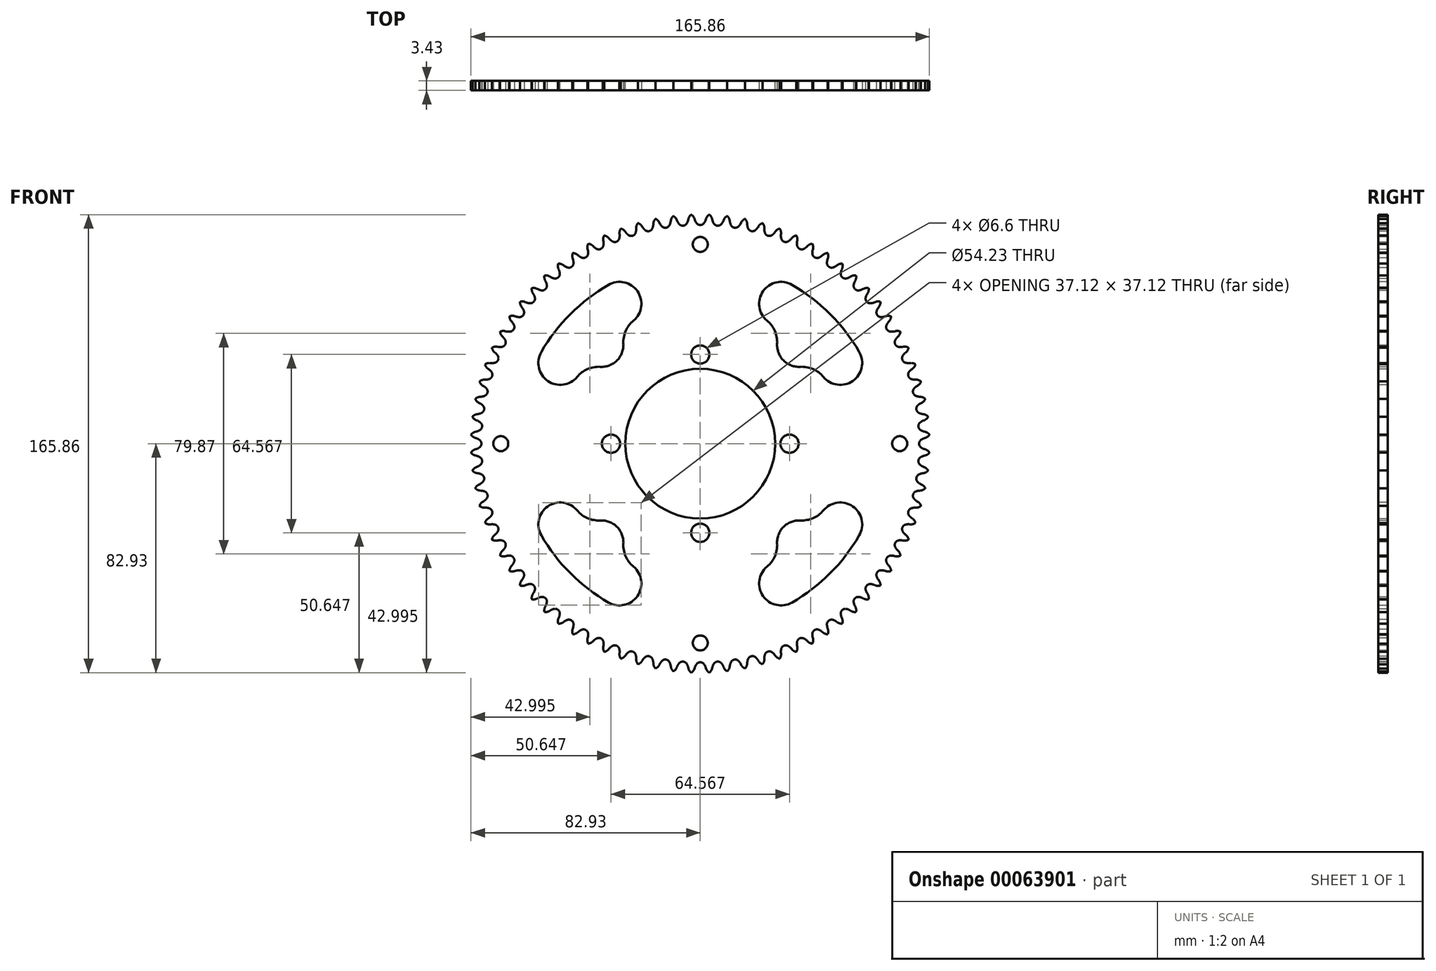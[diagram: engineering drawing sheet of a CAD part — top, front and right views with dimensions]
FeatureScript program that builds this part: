
annotation { "Feature Type Name" : "Feature", "Feature Type Description" : "" }
export const myFeature = defineFeature(function(context is Context, id is Id, definition is map)
    precondition{}
    {
        {
            var Q0;
            Q0=qCreatedBy(makeId("Front.planeOp"),FACE);
            var sketch = newSketch(context, id + "F0", { "sketchPlane" : qUnion([Q0])});
            skCircle(sketch, "E0", {"center": v(0, 0) * mm, "radius": 88.9 * mm});
            skCircle(sketch, "E1", {"center": v(0, 0) * mm, "radius": 27.11 * mm});
            skSolve(sketch);
        }
        {
            var Q0;
            Q0 = qSketchRegion(id + "F0", true);
            extrude(context, id + "F1", {"entities" : qUnion([Q0]), "depth" : 3.43 * mm});
        }
        {
            var Q0;
            Q0=makeQuery(id+"F1.opExtrude","CAP_FACE",FACE,{"disambiguationData":[OSD([sQuery(id+"F0.wireOp",EDGE,"E0"),sQuery(id+"F0.wireOp",EDGE,"E1")])],"isStart":false});
            var sketch = newSketch(context, id + "F2", { "sketchPlane" : qUnion([Q0])});
            skCircle(sketch, "E2", {"center": v(0, 0) * mm, "radius": 80.87 * mm, "construction": true});
            skLineSegment(sketch, "E3", {"start": v(0, 0) * mm, "end": v(0, 80.87) * mm, "construction": true});
            skLineSegment(sketch, "E4", {"start": v(0, 80.87) * mm, "end": v(106.86, 80.87) * mm, "construction": true});
            skLineSegment(sketch, "E5", {"start": v(0, 80.87) * mm, "end": v(2.14, 82.41) * mm, "construction": true});
            skLineSegment(sketch, "E6", {"start": v(2.14, 82.41) * mm, "end": v(-1.97, 81.04) * mm, "construction": true});
            skLineSegment(sketch, "E7", {"start": v(-1.97, 81.04) * mm, "end": v(-1.97, 81.04) * mm});
            skLineSegment(sketch, "E8", {"start": v(0, 0) * mm, "end": v(-3.26, 82.93) * mm, "construction": true});
            skPoint(sketch, "E8.endSnap0", {"position": v(-3.26, 84.9) * mm});
            skArc(sketch, "E9", {"start": v(-2.13, 81.52) * mm, "mid": v(-2.57, 82.33) * mm, "end": v(-3.26, 82.93) * mm});
            skArc(sketch, "E10", {"start": v(-3.26, 82.93) * mm, "mid": v(-6.67, 79.06) * mm, "end": v(-2.13, 81.52) * mm, "construction": true});
            skLineSegment(sketch, "E11", {"start": v(-2.13, 81.52) * mm, "end": v(-4.54, 88.75) * mm, "construction": true});
            skLineSegment(sketch, "E12", {"start": v(-1.97, 81.04) * mm, "end": v(-2.13, 81.52) * mm});
            skArc(sketch, "E13", {"start": v(-1.38, 79.88) * mm, "mid": v(6, 84.4) * mm, "end": v(-1.97, 81.04) * mm, "construction": true});
            skArc(sketch, "E14", {"start": v(-1.97, 81.04) * mm, "mid": v(-1.72, 80.44) * mm, "end": v(-1.38, 79.88) * mm});
            skArc(sketch, "E15.MirrorCS", {"start": v(1.38, 79.88) * mm, "mid": v(-6, 84.4) * mm, "end": v(1.97, 81.04) * mm, "construction": true});
            skArc(sketch, "E16.MirrorCS", {"start": v(2.13, 81.52) * mm, "mid": v(2.57, 82.33) * mm, "end": v(3.26, 82.93) * mm});
            skLineSegment(sketch, "E17.MirrorCS", {"start": v(1.97, 81.04) * mm, "end": v(2.13, 81.52) * mm});
            skArc(sketch, "E18.MirrorCS", {"start": v(1.97, 81.04) * mm, "mid": v(1.72, 80.44) * mm, "end": v(1.38, 79.88) * mm});
            skArc(sketch, "E19", {"start": v(-1.38, 79.88) * mm, "mid": v(0, 79.17) * mm, "end": v(1.38, 79.88) * mm});
            skArc(sketch, "E20", {"start": v(1.38, 79.88) * mm, "mid": v(0, 82.57) * mm, "end": v(-1.38, 79.88) * mm, "construction": true});
            skArc(sketch, "E21.1.0", {"start": v(-8.52, 81.1) * mm, "mid": v(-9.02, 81.87) * mm, "end": v(-9.76, 82.42) * mm});
            skLineSegment(sketch, "E21.1.1", {"start": v(-8.33, 80.64) * mm, "end": v(-8.52, 81.1) * mm});
            skArc(sketch, "E21.1.2", {"start": v(-8.33, 80.64) * mm, "mid": v(-8.03, 80.05) * mm, "end": v(-7.64, 79.52) * mm});
            skArc(sketch, "E21.1.3", {"start": v(-7.64, 79.52) * mm, "mid": v(-6.21, 78.93) * mm, "end": v(-4.9, 79.74) * mm});
            skArc(sketch, "E21.1.4", {"start": v(-4.4, 80.95) * mm, "mid": v(-4.6, 80.32) * mm, "end": v(-4.9, 79.74) * mm});
            skLineSegment(sketch, "E21.1.5", {"start": v(-4.4, 80.95) * mm, "end": v(-4.27, 81.44) * mm});
            skArc(sketch, "E21.1.6", {"start": v(-4.27, 81.44) * mm, "mid": v(-3.9, 82.27) * mm, "end": v(-3.26, 82.93) * mm});
            skArc(sketch, "E21.2.0", {"start": v(-14.86, 80.18) * mm, "mid": v(-15.42, 80.91) * mm, "end": v(-16.2, 81.4) * mm});
            skLineSegment(sketch, "E21.2.1", {"start": v(-14.63, 79.73) * mm, "end": v(-14.86, 80.18) * mm});
            skArc(sketch, "E21.2.2", {"start": v(-14.63, 79.73) * mm, "mid": v(-14.28, 79.18) * mm, "end": v(-13.86, 78.68) * mm});
            skArc(sketch, "E21.2.3", {"start": v(-13.86, 78.68) * mm, "mid": v(-12.39, 78.2) * mm, "end": v(-11.13, 79.11) * mm});
            skArc(sketch, "E21.2.4", {"start": v(-10.73, 80.35) * mm, "mid": v(-10.89, 79.72) * mm, "end": v(-11.13, 79.11) * mm});
            skLineSegment(sketch, "E21.2.5", {"start": v(-10.73, 80.35) * mm, "end": v(-10.65, 80.85) * mm});
            skArc(sketch, "E21.2.6", {"start": v(-10.65, 80.85) * mm, "mid": v(-10.34, 81.71) * mm, "end": v(-9.76, 82.42) * mm});
            skArc(sketch, "E21.3.0", {"start": v(-21.1, 78.77) * mm, "mid": v(-21.72, 79.45) * mm, "end": v(-22.53, 79.88) * mm});
            skLineSegment(sketch, "E21.3.1", {"start": v(-20.84, 78.34) * mm, "end": v(-21.1, 78.77) * mm});
            skArc(sketch, "E21.3.2", {"start": v(-20.84, 78.34) * mm, "mid": v(-20.45, 77.81) * mm, "end": v(-19.99, 77.35) * mm});
            skArc(sketch, "E21.3.3", {"start": v(-19.99, 77.35) * mm, "mid": v(-18.48, 76.99) * mm, "end": v(-17.3, 78) * mm});
            skArc(sketch, "E21.3.4", {"start": v(-17, 79.26) * mm, "mid": v(-17.1, 78.62) * mm, "end": v(-17.3, 78) * mm});
            skLineSegment(sketch, "E21.3.5", {"start": v(-17, 79.26) * mm, "end": v(-16.96, 79.77) * mm});
            skArc(sketch, "E21.3.6", {"start": v(-16.96, 79.77) * mm, "mid": v(-16.72, 80.65) * mm, "end": v(-16.2, 81.4) * mm});
            skArc(sketch, "E21.4.0", {"start": v(-27.22, 76.87) * mm, "mid": v(-27.88, 77.5) * mm, "end": v(-28.73, 77.87) * mm});
            skLineSegment(sketch, "E21.4.1", {"start": v(-26.92, 76.47) * mm, "end": v(-27.22, 76.87) * mm});
            skArc(sketch, "E21.4.2", {"start": v(-26.92, 76.47) * mm, "mid": v(-26.5, 75.97) * mm, "end": v(-26, 75.54) * mm});
            skArc(sketch, "E21.4.3", {"start": v(-26, 75.54) * mm, "mid": v(-24.47, 75.3) * mm, "end": v(-23.37, 76.4) * mm});
            skArc(sketch, "E21.4.4", {"start": v(-23.17, 77.68) * mm, "mid": v(-23.22, 77.03) * mm, "end": v(-23.37, 76.4) * mm});
            skLineSegment(sketch, "E21.4.5", {"start": v(-23.17, 77.68) * mm, "end": v(-23.16, 78.19) * mm});
            skArc(sketch, "E21.4.6", {"start": v(-23.16, 78.19) * mm, "mid": v(-23, 79.1) * mm, "end": v(-22.53, 79.88) * mm});
            skArc(sketch, "E21.5.0", {"start": v(-33.17, 74.5) * mm, "mid": v(-33.88, 75.08) * mm, "end": v(-34.75, 75.37) * mm});
            skLineSegment(sketch, "E21.5.1", {"start": v(-32.84, 74.12) * mm, "end": v(-33.17, 74.5) * mm});
            skArc(sketch, "E21.5.2", {"start": v(-32.84, 74.12) * mm, "mid": v(-32.37, 73.66) * mm, "end": v(-31.84, 73.27) * mm});
            skArc(sketch, "E21.5.3", {"start": v(-31.84, 73.27) * mm, "mid": v(-30.3, 73.15) * mm, "end": v(-29.3, 74.33) * mm});
            skArc(sketch, "E21.5.4", {"start": v(-29.2, 75.63) * mm, "mid": v(-29.2, 74.97) * mm, "end": v(-29.3, 74.33) * mm});
            skLineSegment(sketch, "E21.5.5", {"start": v(-29.2, 75.63) * mm, "end": v(-29.23, 76.13) * mm});
            skArc(sketch, "E21.5.6", {"start": v(-29.23, 76.13) * mm, "mid": v(-29.13, 77.04) * mm, "end": v(-28.73, 77.87) * mm});
            skArc(sketch, "E21.6.0", {"start": v(-38.9, 71.67) * mm, "mid": v(-39.67, 72.19) * mm, "end": v(-40.55, 72.41) * mm});
            skLineSegment(sketch, "E21.6.1", {"start": v(-38.55, 71.31) * mm, "end": v(-38.9, 71.67) * mm});
            skArc(sketch, "E21.6.2", {"start": v(-38.55, 71.31) * mm, "mid": v(-38.05, 70.89) * mm, "end": v(-37.5, 70.55) * mm});
            skArc(sketch, "E21.6.3", {"start": v(-37.5, 70.55) * mm, "mid": v(-35.94, 70.54) * mm, "end": v(-35.04, 71.8) * mm});
            skArc(sketch, "E21.6.4", {"start": v(-35.03, 73.1) * mm, "mid": v(-34.99, 72.45) * mm, "end": v(-35.04, 71.8) * mm});
            skLineSegment(sketch, "E21.6.5", {"start": v(-35.03, 73.1) * mm, "end": v(-35.1, 73.6) * mm});
            skArc(sketch, "E21.6.6", {"start": v(-35.1, 73.6) * mm, "mid": v(-35.09, 74.52) * mm, "end": v(-34.75, 75.37) * mm});
            skArc(sketch, "E21.7.0", {"start": v(-44.41, 68.4) * mm, "mid": v(-45.2, 68.85) * mm, "end": v(-46.11, 69) * mm});
            skLineSegment(sketch, "E21.7.1", {"start": v(-44.03, 68.07) * mm, "end": v(-44.41, 68.4) * mm});
            skArc(sketch, "E21.7.2", {"start": v(-44.03, 68.07) * mm, "mid": v(-43.5, 67.69) * mm, "end": v(-42.91, 67.39) * mm});
            skArc(sketch, "E21.7.3", {"start": v(-42.91, 67.39) * mm, "mid": v(-41.37, 67.5) * mm, "end": v(-40.56, 68.83) * mm});
            skArc(sketch, "E21.7.4", {"start": v(-40.66, 70.13) * mm, "mid": v(-40.56, 69.48) * mm, "end": v(-40.56, 68.83) * mm});
            skLineSegment(sketch, "E21.7.5", {"start": v(-40.66, 70.13) * mm, "end": v(-40.78, 70.62) * mm});
            skArc(sketch, "E21.7.6", {"start": v(-40.78, 70.62) * mm, "mid": v(-40.82, 71.54) * mm, "end": v(-40.55, 72.41) * mm});
            skArc(sketch, "E21.8.0", {"start": v(-49.64, 64.7) * mm, "mid": v(-50.47, 65.1) * mm, "end": v(-51.38, 65.18) * mm});
            skLineSegment(sketch, "E21.8.1", {"start": v(-49.23, 64.4) * mm, "end": v(-49.64, 64.7) * mm});
            skArc(sketch, "E21.8.2", {"start": v(-49.23, 64.4) * mm, "mid": v(-48.67, 64.06) * mm, "end": v(-48.07, 63.81) * mm});
            skArc(sketch, "E21.8.3", {"start": v(-48.07, 63.81) * mm, "mid": v(-46.54, 64.05) * mm, "end": v(-45.84, 65.43) * mm});
            skArc(sketch, "E21.8.4", {"start": v(-46.04, 66.72) * mm, "mid": v(-45.89, 66.09) * mm, "end": v(-45.84, 65.43) * mm});
            skLineSegment(sketch, "E21.8.5", {"start": v(-46.04, 66.72) * mm, "end": v(-46.2, 67.2) * mm});
            skArc(sketch, "E21.8.6", {"start": v(-46.2, 67.2) * mm, "mid": v(-46.31, 68.11) * mm, "end": v(-46.11, 69) * mm});
            skArc(sketch, "E21.9.0", {"start": v(-54.57, 60.6) * mm, "mid": v(-55.42, 60.93) * mm, "end": v(-56.34, 60.95) * mm});
            skLineSegment(sketch, "E21.9.1", {"start": v(-54.13, 60.34) * mm, "end": v(-54.57, 60.6) * mm});
            skArc(sketch, "E21.9.2", {"start": v(-54.13, 60.34) * mm, "mid": v(-53.55, 60.05) * mm, "end": v(-52.93, 59.85) * mm});
            skArc(sketch, "E21.9.3", {"start": v(-52.93, 59.85) * mm, "mid": v(-51.42, 60.2) * mm, "end": v(-50.83, 61.64) * mm});
            skArc(sketch, "E21.9.4", {"start": v(-51.13, 62.9) * mm, "mid": v(-50.93, 62.28) * mm, "end": v(-50.83, 61.64) * mm});
            skLineSegment(sketch, "E21.9.5", {"start": v(-51.13, 62.9) * mm, "end": v(-51.32, 63.37) * mm});
            skArc(sketch, "E21.9.6", {"start": v(-51.32, 63.37) * mm, "mid": v(-51.51, 64.27) * mm, "end": v(-51.38, 65.18) * mm});
            skArc(sketch, "E21.10.0", {"start": v(-59.15, 56.14) * mm, "mid": v(-60.03, 56.4) * mm, "end": v(-60.95, 56.34) * mm});
            skLineSegment(sketch, "E21.10.1", {"start": v(-58.7, 55.9) * mm, "end": v(-59.15, 56.14) * mm});
            skArc(sketch, "E21.10.2", {"start": v(-58.7, 55.9) * mm, "mid": v(-58.1, 55.66) * mm, "end": v(-57.46, 55.5) * mm});
            skArc(sketch, "E21.10.3", {"start": v(-57.46, 55.5) * mm, "mid": v(-55.98, 55.98) * mm, "end": v(-55.5, 57.46) * mm});
            skArc(sketch, "E21.10.4", {"start": v(-55.9, 58.7) * mm, "mid": v(-55.66, 58.1) * mm, "end": v(-55.5, 57.46) * mm});
            skLineSegment(sketch, "E21.10.5", {"start": v(-55.9, 58.7) * mm, "end": v(-56.14, 59.15) * mm});
            skArc(sketch, "E21.10.6", {"start": v(-56.14, 59.15) * mm, "mid": v(-56.4, 60.03) * mm, "end": v(-56.34, 60.95) * mm});
            skArc(sketch, "E21.11.0", {"start": v(-63.37, 51.32) * mm, "mid": v(-64.27, 51.51) * mm, "end": v(-65.18, 51.38) * mm});
            skLineSegment(sketch, "E21.11.1", {"start": v(-62.9, 51.13) * mm, "end": v(-63.37, 51.32) * mm});
            skArc(sketch, "E21.11.2", {"start": v(-62.9, 51.13) * mm, "mid": v(-62.28, 50.93) * mm, "end": v(-61.64, 50.83) * mm});
            skArc(sketch, "E21.11.3", {"start": v(-61.64, 50.83) * mm, "mid": v(-60.2, 51.42) * mm, "end": v(-59.85, 52.93) * mm});
            skArc(sketch, "E21.11.4", {"start": v(-60.34, 54.13) * mm, "mid": v(-60.05, 53.55) * mm, "end": v(-59.85, 52.93) * mm});
            skLineSegment(sketch, "E21.11.5", {"start": v(-60.34, 54.13) * mm, "end": v(-60.6, 54.57) * mm});
            skArc(sketch, "E21.11.6", {"start": v(-60.6, 54.57) * mm, "mid": v(-60.93, 55.42) * mm, "end": v(-60.95, 56.34) * mm});
            skArc(sketch, "E21.12.0", {"start": v(-67.2, 46.2) * mm, "mid": v(-68.11, 46.31) * mm, "end": v(-69, 46.11) * mm});
            skLineSegment(sketch, "E21.12.1", {"start": v(-66.72, 46.04) * mm, "end": v(-67.2, 46.2) * mm});
            skArc(sketch, "E21.12.2", {"start": v(-66.72, 46.04) * mm, "mid": v(-66.09, 45.89) * mm, "end": v(-65.43, 45.84) * mm});
            skArc(sketch, "E21.12.3", {"start": v(-65.43, 45.84) * mm, "mid": v(-64.05, 46.54) * mm, "end": v(-63.81, 48.07) * mm});
            skArc(sketch, "E21.12.4", {"start": v(-64.4, 49.23) * mm, "mid": v(-64.06, 48.67) * mm, "end": v(-63.81, 48.07) * mm});
            skLineSegment(sketch, "E21.12.5", {"start": v(-64.4, 49.23) * mm, "end": v(-64.7, 49.64) * mm});
            skArc(sketch, "E21.12.6", {"start": v(-64.7, 49.64) * mm, "mid": v(-65.1, 50.47) * mm, "end": v(-65.18, 51.38) * mm});
            skArc(sketch, "E21.13.0", {"start": v(-70.62, 40.78) * mm, "mid": v(-71.54, 40.82) * mm, "end": v(-72.41, 40.55) * mm});
            skLineSegment(sketch, "E21.13.1", {"start": v(-70.13, 40.66) * mm, "end": v(-70.62, 40.78) * mm});
            skArc(sketch, "E21.13.2", {"start": v(-70.13, 40.66) * mm, "mid": v(-69.48, 40.56) * mm, "end": v(-68.83, 40.56) * mm});
            skArc(sketch, "E21.13.3", {"start": v(-68.83, 40.56) * mm, "mid": v(-67.5, 41.37) * mm, "end": v(-67.39, 42.91) * mm});
            skArc(sketch, "E21.13.4", {"start": v(-68.07, 44.03) * mm, "mid": v(-67.69, 43.5) * mm, "end": v(-67.39, 42.91) * mm});
            skLineSegment(sketch, "E21.13.5", {"start": v(-68.07, 44.03) * mm, "end": v(-68.4, 44.41) * mm});
            skArc(sketch, "E21.13.6", {"start": v(-68.4, 44.41) * mm, "mid": v(-68.85, 45.2) * mm, "end": v(-69, 46.11) * mm});
            skArc(sketch, "E21.14.0", {"start": v(-73.6, 35.1) * mm, "mid": v(-74.52, 35.09) * mm, "end": v(-75.37, 34.75) * mm});
            skLineSegment(sketch, "E21.14.1", {"start": v(-73.1, 35.03) * mm, "end": v(-73.6, 35.1) * mm});
            skArc(sketch, "E21.14.2", {"start": v(-73.1, 35.03) * mm, "mid": v(-72.45, 34.99) * mm, "end": v(-71.8, 35.04) * mm});
            skArc(sketch, "E21.14.3", {"start": v(-71.8, 35.04) * mm, "mid": v(-70.54, 35.94) * mm, "end": v(-70.55, 37.5) * mm});
            skArc(sketch, "E21.14.4", {"start": v(-71.31, 38.55) * mm, "mid": v(-70.89, 38.05) * mm, "end": v(-70.55, 37.5) * mm});
            skLineSegment(sketch, "E21.14.5", {"start": v(-71.31, 38.55) * mm, "end": v(-71.67, 38.9) * mm});
            skArc(sketch, "E21.14.6", {"start": v(-71.67, 38.9) * mm, "mid": v(-72.19, 39.67) * mm, "end": v(-72.41, 40.55) * mm});
            skArc(sketch, "E21.15.0", {"start": v(-76.13, 29.23) * mm, "mid": v(-77.04, 29.13) * mm, "end": v(-77.87, 28.73) * mm});
            skLineSegment(sketch, "E21.15.1", {"start": v(-75.63, 29.2) * mm, "end": v(-76.13, 29.23) * mm});
            skArc(sketch, "E21.15.2", {"start": v(-75.63, 29.2) * mm, "mid": v(-74.97, 29.2) * mm, "end": v(-74.33, 29.3) * mm});
            skArc(sketch, "E21.15.3", {"start": v(-74.33, 29.3) * mm, "mid": v(-73.15, 30.3) * mm, "end": v(-73.27, 31.84) * mm});
            skArc(sketch, "E21.15.4", {"start": v(-74.12, 32.84) * mm, "mid": v(-73.66, 32.37) * mm, "end": v(-73.27, 31.84) * mm});
            skLineSegment(sketch, "E21.15.5", {"start": v(-74.12, 32.84) * mm, "end": v(-74.5, 33.17) * mm});
            skArc(sketch, "E21.15.6", {"start": v(-74.5, 33.17) * mm, "mid": v(-75.08, 33.88) * mm, "end": v(-75.37, 34.75) * mm});
            skArc(sketch, "E21.16.0", {"start": v(-78.19, 23.16) * mm, "mid": v(-79.1, 23) * mm, "end": v(-79.88, 22.53) * mm});
            skLineSegment(sketch, "E21.16.1", {"start": v(-77.68, 23.17) * mm, "end": v(-78.19, 23.16) * mm});
            skArc(sketch, "E21.16.2", {"start": v(-77.68, 23.17) * mm, "mid": v(-77.03, 23.22) * mm, "end": v(-76.4, 23.37) * mm});
            skArc(sketch, "E21.16.3", {"start": v(-76.4, 23.37) * mm, "mid": v(-75.3, 24.47) * mm, "end": v(-75.54, 26) * mm});
            skArc(sketch, "E21.16.4", {"start": v(-76.47, 26.92) * mm, "mid": v(-75.97, 26.5) * mm, "end": v(-75.54, 26) * mm});
            skLineSegment(sketch, "E21.16.5", {"start": v(-76.47, 26.92) * mm, "end": v(-76.87, 27.22) * mm});
            skArc(sketch, "E21.16.6", {"start": v(-76.87, 27.22) * mm, "mid": v(-77.5, 27.88) * mm, "end": v(-77.87, 28.73) * mm});
            skArc(sketch, "E21.17.0", {"start": v(-79.77, 16.96) * mm, "mid": v(-80.65, 16.72) * mm, "end": v(-81.4, 16.2) * mm});
            skLineSegment(sketch, "E21.17.1", {"start": v(-79.26, 17) * mm, "end": v(-79.77, 16.96) * mm});
            skArc(sketch, "E21.17.2", {"start": v(-79.26, 17) * mm, "mid": v(-78.62, 17.1) * mm, "end": v(-78, 17.3) * mm});
            skArc(sketch, "E21.17.3", {"start": v(-78, 17.3) * mm, "mid": v(-76.99, 18.48) * mm, "end": v(-77.35, 19.99) * mm});
            skArc(sketch, "E21.17.4", {"start": v(-78.34, 20.84) * mm, "mid": v(-77.81, 20.45) * mm, "end": v(-77.35, 19.99) * mm});
            skLineSegment(sketch, "E21.17.5", {"start": v(-78.34, 20.84) * mm, "end": v(-78.77, 21.1) * mm});
            skArc(sketch, "E21.17.6", {"start": v(-78.77, 21.1) * mm, "mid": v(-79.45, 21.72) * mm, "end": v(-79.88, 22.53) * mm});
            skArc(sketch, "E21.18.0", {"start": v(-80.85, 10.65) * mm, "mid": v(-81.71, 10.34) * mm, "end": v(-82.42, 9.76) * mm});
            skLineSegment(sketch, "E21.18.1", {"start": v(-80.35, 10.73) * mm, "end": v(-80.85, 10.65) * mm});
            skArc(sketch, "E21.18.2", {"start": v(-80.35, 10.73) * mm, "mid": v(-79.72, 10.89) * mm, "end": v(-79.11, 11.13) * mm});
            skArc(sketch, "E21.18.3", {"start": v(-79.11, 11.13) * mm, "mid": v(-78.2, 12.39) * mm, "end": v(-78.68, 13.86) * mm});
            skArc(sketch, "E21.18.4", {"start": v(-79.73, 14.63) * mm, "mid": v(-79.18, 14.28) * mm, "end": v(-78.68, 13.86) * mm});
            skLineSegment(sketch, "E21.18.5", {"start": v(-79.73, 14.63) * mm, "end": v(-80.18, 14.86) * mm});
            skArc(sketch, "E21.18.6", {"start": v(-80.18, 14.86) * mm, "mid": v(-80.91, 15.42) * mm, "end": v(-81.4, 16.2) * mm});
            skArc(sketch, "E21.19.0", {"start": v(-81.44, 4.27) * mm, "mid": v(-82.27, 3.9) * mm, "end": v(-82.93, 3.26) * mm});
            skLineSegment(sketch, "E21.19.1", {"start": v(-80.95, 4.4) * mm, "end": v(-81.44, 4.27) * mm});
            skArc(sketch, "E21.19.2", {"start": v(-80.95, 4.4) * mm, "mid": v(-80.32, 4.6) * mm, "end": v(-79.74, 4.9) * mm});
            skArc(sketch, "E21.19.3", {"start": v(-79.74, 4.9) * mm, "mid": v(-78.93, 6.21) * mm, "end": v(-79.52, 7.64) * mm});
            skArc(sketch, "E21.19.4", {"start": v(-80.64, 8.33) * mm, "mid": v(-80.05, 8.03) * mm, "end": v(-79.52, 7.64) * mm});
            skLineSegment(sketch, "E21.19.5", {"start": v(-80.64, 8.33) * mm, "end": v(-81.1, 8.52) * mm});
            skArc(sketch, "E21.19.6", {"start": v(-81.1, 8.52) * mm, "mid": v(-81.87, 9.02) * mm, "end": v(-82.42, 9.76) * mm});
            skArc(sketch, "E21.20.0", {"start": v(-81.52, -2.13) * mm, "mid": v(-82.33, -2.57) * mm, "end": v(-82.93, -3.26) * mm});
            skLineSegment(sketch, "E21.20.1", {"start": v(-81.04, -1.97) * mm, "end": v(-81.52, -2.13) * mm});
            skArc(sketch, "E21.20.2", {"start": v(-81.04, -1.97) * mm, "mid": v(-80.44, -1.72) * mm, "end": v(-79.88, -1.38) * mm});
            skArc(sketch, "E21.20.3", {"start": v(-79.88, -1.38) * mm, "mid": v(-79.17, 0) * mm, "end": v(-79.88, 1.38) * mm});
            skArc(sketch, "E21.20.4", {"start": v(-81.04, 1.97) * mm, "mid": v(-80.44, 1.72) * mm, "end": v(-79.88, 1.38) * mm});
            skLineSegment(sketch, "E21.20.5", {"start": v(-81.04, 1.97) * mm, "end": v(-81.52, 2.13) * mm});
            skArc(sketch, "E21.20.6", {"start": v(-81.52, 2.13) * mm, "mid": v(-82.33, 2.57) * mm, "end": v(-82.93, 3.26) * mm});
            skArc(sketch, "E21.21.0", {"start": v(-81.1, -8.52) * mm, "mid": v(-81.87, -9.02) * mm, "end": v(-82.42, -9.76) * mm});
            skLineSegment(sketch, "E21.21.1", {"start": v(-80.64, -8.33) * mm, "end": v(-81.1, -8.52) * mm});
            skArc(sketch, "E21.21.2", {"start": v(-80.64, -8.33) * mm, "mid": v(-80.05, -8.03) * mm, "end": v(-79.52, -7.64) * mm});
            skArc(sketch, "E21.21.3", {"start": v(-79.52, -7.64) * mm, "mid": v(-78.93, -6.21) * mm, "end": v(-79.74, -4.9) * mm});
            skArc(sketch, "E21.21.4", {"start": v(-80.95, -4.4) * mm, "mid": v(-80.32, -4.6) * mm, "end": v(-79.74, -4.9) * mm});
            skLineSegment(sketch, "E21.21.5", {"start": v(-80.95, -4.4) * mm, "end": v(-81.44, -4.27) * mm});
            skArc(sketch, "E21.21.6", {"start": v(-81.44, -4.27) * mm, "mid": v(-82.27, -3.9) * mm, "end": v(-82.93, -3.26) * mm});
            skArc(sketch, "E21.22.0", {"start": v(-80.18, -14.86) * mm, "mid": v(-80.91, -15.42) * mm, "end": v(-81.4, -16.2) * mm});
            skLineSegment(sketch, "E21.22.1", {"start": v(-79.73, -14.63) * mm, "end": v(-80.18, -14.86) * mm});
            skArc(sketch, "E21.22.2", {"start": v(-79.73, -14.63) * mm, "mid": v(-79.18, -14.28) * mm, "end": v(-78.68, -13.86) * mm});
            skArc(sketch, "E21.22.3", {"start": v(-78.68, -13.86) * mm, "mid": v(-78.2, -12.39) * mm, "end": v(-79.11, -11.13) * mm});
            skArc(sketch, "E21.22.4", {"start": v(-80.35, -10.73) * mm, "mid": v(-79.72, -10.89) * mm, "end": v(-79.11, -11.13) * mm});
            skLineSegment(sketch, "E21.22.5", {"start": v(-80.35, -10.73) * mm, "end": v(-80.85, -10.65) * mm});
            skArc(sketch, "E21.22.6", {"start": v(-80.85, -10.65) * mm, "mid": v(-81.71, -10.34) * mm, "end": v(-82.42, -9.76) * mm});
            skArc(sketch, "E21.23.0", {"start": v(-78.77, -21.1) * mm, "mid": v(-79.45, -21.72) * mm, "end": v(-79.88, -22.53) * mm});
            skLineSegment(sketch, "E21.23.1", {"start": v(-78.34, -20.84) * mm, "end": v(-78.77, -21.1) * mm});
            skArc(sketch, "E21.23.2", {"start": v(-78.34, -20.84) * mm, "mid": v(-77.81, -20.45) * mm, "end": v(-77.35, -19.99) * mm});
            skArc(sketch, "E21.23.3", {"start": v(-77.35, -19.99) * mm, "mid": v(-76.99, -18.48) * mm, "end": v(-78, -17.3) * mm});
            skArc(sketch, "E21.23.4", {"start": v(-79.26, -17) * mm, "mid": v(-78.62, -17.1) * mm, "end": v(-78, -17.3) * mm});
            skLineSegment(sketch, "E21.23.5", {"start": v(-79.26, -17) * mm, "end": v(-79.77, -16.96) * mm});
            skArc(sketch, "E21.23.6", {"start": v(-79.77, -16.96) * mm, "mid": v(-80.65, -16.72) * mm, "end": v(-81.4, -16.2) * mm});
            skArc(sketch, "E21.24.0", {"start": v(-76.87, -27.22) * mm, "mid": v(-77.5, -27.88) * mm, "end": v(-77.87, -28.73) * mm});
            skLineSegment(sketch, "E21.24.1", {"start": v(-76.47, -26.92) * mm, "end": v(-76.87, -27.22) * mm});
            skArc(sketch, "E21.24.2", {"start": v(-76.47, -26.92) * mm, "mid": v(-75.97, -26.5) * mm, "end": v(-75.54, -26) * mm});
            skArc(sketch, "E21.24.3", {"start": v(-75.54, -26) * mm, "mid": v(-75.3, -24.47) * mm, "end": v(-76.4, -23.37) * mm});
            skArc(sketch, "E21.24.4", {"start": v(-77.68, -23.17) * mm, "mid": v(-77.03, -23.22) * mm, "end": v(-76.4, -23.37) * mm});
            skLineSegment(sketch, "E21.24.5", {"start": v(-77.68, -23.17) * mm, "end": v(-78.19, -23.16) * mm});
            skArc(sketch, "E21.24.6", {"start": v(-78.19, -23.16) * mm, "mid": v(-79.1, -23) * mm, "end": v(-79.88, -22.53) * mm});
            skArc(sketch, "E21.25.0", {"start": v(-74.5, -33.17) * mm, "mid": v(-75.08, -33.88) * mm, "end": v(-75.37, -34.75) * mm});
            skLineSegment(sketch, "E21.25.1", {"start": v(-74.12, -32.84) * mm, "end": v(-74.5, -33.17) * mm});
            skArc(sketch, "E21.25.2", {"start": v(-74.12, -32.84) * mm, "mid": v(-73.66, -32.37) * mm, "end": v(-73.27, -31.84) * mm});
            skArc(sketch, "E21.25.3", {"start": v(-73.27, -31.84) * mm, "mid": v(-73.15, -30.3) * mm, "end": v(-74.33, -29.3) * mm});
            skArc(sketch, "E21.25.4", {"start": v(-75.63, -29.2) * mm, "mid": v(-74.97, -29.2) * mm, "end": v(-74.33, -29.3) * mm});
            skLineSegment(sketch, "E21.25.5", {"start": v(-75.63, -29.2) * mm, "end": v(-76.13, -29.23) * mm});
            skArc(sketch, "E21.25.6", {"start": v(-76.13, -29.23) * mm, "mid": v(-77.04, -29.13) * mm, "end": v(-77.87, -28.73) * mm});
            skArc(sketch, "E21.26.0", {"start": v(-71.67, -38.9) * mm, "mid": v(-72.19, -39.67) * mm, "end": v(-72.41, -40.55) * mm});
            skLineSegment(sketch, "E21.26.1", {"start": v(-71.31, -38.55) * mm, "end": v(-71.67, -38.9) * mm});
            skArc(sketch, "E21.26.2", {"start": v(-71.31, -38.55) * mm, "mid": v(-70.89, -38.05) * mm, "end": v(-70.55, -37.5) * mm});
            skArc(sketch, "E21.26.3", {"start": v(-70.55, -37.5) * mm, "mid": v(-70.54, -35.94) * mm, "end": v(-71.8, -35.04) * mm});
            skArc(sketch, "E21.26.4", {"start": v(-73.1, -35.03) * mm, "mid": v(-72.45, -34.99) * mm, "end": v(-71.8, -35.04) * mm});
            skLineSegment(sketch, "E21.26.5", {"start": v(-73.1, -35.03) * mm, "end": v(-73.6, -35.1) * mm});
            skArc(sketch, "E21.26.6", {"start": v(-73.6, -35.1) * mm, "mid": v(-74.52, -35.09) * mm, "end": v(-75.37, -34.75) * mm});
            skArc(sketch, "E21.27.0", {"start": v(-68.4, -44.41) * mm, "mid": v(-68.85, -45.2) * mm, "end": v(-69, -46.11) * mm});
            skLineSegment(sketch, "E21.27.1", {"start": v(-68.07, -44.03) * mm, "end": v(-68.4, -44.41) * mm});
            skArc(sketch, "E21.27.2", {"start": v(-68.07, -44.03) * mm, "mid": v(-67.69, -43.5) * mm, "end": v(-67.39, -42.91) * mm});
            skArc(sketch, "E21.27.3", {"start": v(-67.39, -42.91) * mm, "mid": v(-67.5, -41.37) * mm, "end": v(-68.83, -40.56) * mm});
            skArc(sketch, "E21.27.4", {"start": v(-70.13, -40.66) * mm, "mid": v(-69.48, -40.56) * mm, "end": v(-68.83, -40.56) * mm});
            skLineSegment(sketch, "E21.27.5", {"start": v(-70.13, -40.66) * mm, "end": v(-70.62, -40.78) * mm});
            skArc(sketch, "E21.27.6", {"start": v(-70.62, -40.78) * mm, "mid": v(-71.54, -40.82) * mm, "end": v(-72.41, -40.55) * mm});
            skArc(sketch, "E21.28.0", {"start": v(-64.7, -49.64) * mm, "mid": v(-65.1, -50.47) * mm, "end": v(-65.18, -51.38) * mm});
            skLineSegment(sketch, "E21.28.1", {"start": v(-64.4, -49.23) * mm, "end": v(-64.7, -49.64) * mm});
            skArc(sketch, "E21.28.2", {"start": v(-64.4, -49.23) * mm, "mid": v(-64.06, -48.67) * mm, "end": v(-63.81, -48.07) * mm});
            skArc(sketch, "E21.28.3", {"start": v(-63.81, -48.07) * mm, "mid": v(-64.05, -46.54) * mm, "end": v(-65.43, -45.84) * mm});
            skArc(sketch, "E21.28.4", {"start": v(-66.72, -46.04) * mm, "mid": v(-66.09, -45.89) * mm, "end": v(-65.43, -45.84) * mm});
            skLineSegment(sketch, "E21.28.5", {"start": v(-66.72, -46.04) * mm, "end": v(-67.2, -46.2) * mm});
            skArc(sketch, "E21.28.6", {"start": v(-67.2, -46.2) * mm, "mid": v(-68.11, -46.31) * mm, "end": v(-69, -46.11) * mm});
            skArc(sketch, "E21.29.0", {"start": v(-60.6, -54.57) * mm, "mid": v(-60.93, -55.42) * mm, "end": v(-60.95, -56.34) * mm});
            skLineSegment(sketch, "E21.29.1", {"start": v(-60.34, -54.13) * mm, "end": v(-60.6, -54.57) * mm});
            skArc(sketch, "E21.29.2", {"start": v(-60.34, -54.13) * mm, "mid": v(-60.05, -53.55) * mm, "end": v(-59.85, -52.93) * mm});
            skArc(sketch, "E21.29.3", {"start": v(-59.85, -52.93) * mm, "mid": v(-60.2, -51.42) * mm, "end": v(-61.64, -50.83) * mm});
            skArc(sketch, "E21.29.4", {"start": v(-62.9, -51.13) * mm, "mid": v(-62.28, -50.93) * mm, "end": v(-61.64, -50.83) * mm});
            skLineSegment(sketch, "E21.29.5", {"start": v(-62.9, -51.13) * mm, "end": v(-63.37, -51.32) * mm});
            skArc(sketch, "E21.29.6", {"start": v(-63.37, -51.32) * mm, "mid": v(-64.27, -51.51) * mm, "end": v(-65.18, -51.38) * mm});
            skArc(sketch, "E21.30.0", {"start": v(-56.14, -59.15) * mm, "mid": v(-56.4, -60.03) * mm, "end": v(-56.34, -60.95) * mm});
            skLineSegment(sketch, "E21.30.1", {"start": v(-55.9, -58.7) * mm, "end": v(-56.14, -59.15) * mm});
            skArc(sketch, "E21.30.2", {"start": v(-55.9, -58.7) * mm, "mid": v(-55.66, -58.1) * mm, "end": v(-55.5, -57.46) * mm});
            skArc(sketch, "E21.30.3", {"start": v(-55.5, -57.46) * mm, "mid": v(-55.98, -55.98) * mm, "end": v(-57.46, -55.5) * mm});
            skArc(sketch, "E21.30.4", {"start": v(-58.7, -55.9) * mm, "mid": v(-58.1, -55.66) * mm, "end": v(-57.46, -55.5) * mm});
            skLineSegment(sketch, "E21.30.5", {"start": v(-58.7, -55.9) * mm, "end": v(-59.15, -56.14) * mm});
            skArc(sketch, "E21.30.6", {"start": v(-59.15, -56.14) * mm, "mid": v(-60.03, -56.4) * mm, "end": v(-60.95, -56.34) * mm});
            skArc(sketch, "E21.31.0", {"start": v(-51.32, -63.37) * mm, "mid": v(-51.51, -64.27) * mm, "end": v(-51.38, -65.18) * mm});
            skLineSegment(sketch, "E21.31.1", {"start": v(-51.13, -62.9) * mm, "end": v(-51.32, -63.37) * mm});
            skArc(sketch, "E21.31.2", {"start": v(-51.13, -62.9) * mm, "mid": v(-50.93, -62.28) * mm, "end": v(-50.83, -61.64) * mm});
            skArc(sketch, "E21.31.3", {"start": v(-50.83, -61.64) * mm, "mid": v(-51.42, -60.2) * mm, "end": v(-52.93, -59.85) * mm});
            skArc(sketch, "E21.31.4", {"start": v(-54.13, -60.34) * mm, "mid": v(-53.55, -60.05) * mm, "end": v(-52.93, -59.85) * mm});
            skLineSegment(sketch, "E21.31.5", {"start": v(-54.13, -60.34) * mm, "end": v(-54.57, -60.6) * mm});
            skArc(sketch, "E21.31.6", {"start": v(-54.57, -60.6) * mm, "mid": v(-55.42, -60.93) * mm, "end": v(-56.34, -60.95) * mm});
            skArc(sketch, "E21.32.0", {"start": v(-46.2, -67.2) * mm, "mid": v(-46.31, -68.11) * mm, "end": v(-46.11, -69) * mm});
            skLineSegment(sketch, "E21.32.1", {"start": v(-46.04, -66.72) * mm, "end": v(-46.2, -67.2) * mm});
            skArc(sketch, "E21.32.2", {"start": v(-46.04, -66.72) * mm, "mid": v(-45.89, -66.09) * mm, "end": v(-45.84, -65.43) * mm});
            skArc(sketch, "E21.32.3", {"start": v(-45.84, -65.43) * mm, "mid": v(-46.54, -64.05) * mm, "end": v(-48.07, -63.81) * mm});
            skArc(sketch, "E21.32.4", {"start": v(-49.23, -64.4) * mm, "mid": v(-48.67, -64.06) * mm, "end": v(-48.07, -63.81) * mm});
            skLineSegment(sketch, "E21.32.5", {"start": v(-49.23, -64.4) * mm, "end": v(-49.64, -64.7) * mm});
            skArc(sketch, "E21.32.6", {"start": v(-49.64, -64.7) * mm, "mid": v(-50.47, -65.1) * mm, "end": v(-51.38, -65.18) * mm});
            skArc(sketch, "E21.33.0", {"start": v(-40.78, -70.62) * mm, "mid": v(-40.82, -71.54) * mm, "end": v(-40.55, -72.41) * mm});
            skLineSegment(sketch, "E21.33.1", {"start": v(-40.66, -70.13) * mm, "end": v(-40.78, -70.62) * mm});
            skArc(sketch, "E21.33.2", {"start": v(-40.66, -70.13) * mm, "mid": v(-40.56, -69.48) * mm, "end": v(-40.56, -68.83) * mm});
            skArc(sketch, "E21.33.3", {"start": v(-40.56, -68.83) * mm, "mid": v(-41.37, -67.5) * mm, "end": v(-42.91, -67.39) * mm});
            skArc(sketch, "E21.33.4", {"start": v(-44.03, -68.07) * mm, "mid": v(-43.5, -67.69) * mm, "end": v(-42.91, -67.39) * mm});
            skLineSegment(sketch, "E21.33.5", {"start": v(-44.03, -68.07) * mm, "end": v(-44.41, -68.4) * mm});
            skArc(sketch, "E21.33.6", {"start": v(-44.41, -68.4) * mm, "mid": v(-45.2, -68.85) * mm, "end": v(-46.11, -69) * mm});
            skArc(sketch, "E21.34.0", {"start": v(-35.1, -73.6) * mm, "mid": v(-35.09, -74.52) * mm, "end": v(-34.75, -75.37) * mm});
            skLineSegment(sketch, "E21.34.1", {"start": v(-35.03, -73.1) * mm, "end": v(-35.1, -73.6) * mm});
            skArc(sketch, "E21.34.2", {"start": v(-35.03, -73.1) * mm, "mid": v(-34.99, -72.45) * mm, "end": v(-35.04, -71.8) * mm});
            skArc(sketch, "E21.34.3", {"start": v(-35.04, -71.8) * mm, "mid": v(-35.94, -70.54) * mm, "end": v(-37.5, -70.55) * mm});
            skArc(sketch, "E21.34.4", {"start": v(-38.55, -71.31) * mm, "mid": v(-38.05, -70.89) * mm, "end": v(-37.5, -70.55) * mm});
            skLineSegment(sketch, "E21.34.5", {"start": v(-38.55, -71.31) * mm, "end": v(-38.9, -71.67) * mm});
            skArc(sketch, "E21.34.6", {"start": v(-38.9, -71.67) * mm, "mid": v(-39.67, -72.19) * mm, "end": v(-40.55, -72.41) * mm});
            skArc(sketch, "E21.35.0", {"start": v(-29.23, -76.13) * mm, "mid": v(-29.13, -77.04) * mm, "end": v(-28.73, -77.87) * mm});
            skLineSegment(sketch, "E21.35.1", {"start": v(-29.2, -75.63) * mm, "end": v(-29.23, -76.13) * mm});
            skArc(sketch, "E21.35.2", {"start": v(-29.2, -75.63) * mm, "mid": v(-29.2, -74.97) * mm, "end": v(-29.3, -74.33) * mm});
            skArc(sketch, "E21.35.3", {"start": v(-29.3, -74.33) * mm, "mid": v(-30.3, -73.15) * mm, "end": v(-31.84, -73.27) * mm});
            skArc(sketch, "E21.35.4", {"start": v(-32.84, -74.12) * mm, "mid": v(-32.37, -73.66) * mm, "end": v(-31.84, -73.27) * mm});
            skLineSegment(sketch, "E21.35.5", {"start": v(-32.84, -74.12) * mm, "end": v(-33.17, -74.5) * mm});
            skArc(sketch, "E21.35.6", {"start": v(-33.17, -74.5) * mm, "mid": v(-33.88, -75.08) * mm, "end": v(-34.75, -75.37) * mm});
            skArc(sketch, "E21.36.0", {"start": v(-23.16, -78.19) * mm, "mid": v(-23, -79.1) * mm, "end": v(-22.53, -79.88) * mm});
            skLineSegment(sketch, "E21.36.1", {"start": v(-23.17, -77.68) * mm, "end": v(-23.16, -78.19) * mm});
            skArc(sketch, "E21.36.2", {"start": v(-23.17, -77.68) * mm, "mid": v(-23.22, -77.03) * mm, "end": v(-23.37, -76.4) * mm});
            skArc(sketch, "E21.36.3", {"start": v(-23.37, -76.4) * mm, "mid": v(-24.47, -75.3) * mm, "end": v(-26, -75.54) * mm});
            skArc(sketch, "E21.36.4", {"start": v(-26.92, -76.47) * mm, "mid": v(-26.5, -75.97) * mm, "end": v(-26, -75.54) * mm});
            skLineSegment(sketch, "E21.36.5", {"start": v(-26.92, -76.47) * mm, "end": v(-27.22, -76.87) * mm});
            skArc(sketch, "E21.36.6", {"start": v(-27.22, -76.87) * mm, "mid": v(-27.88, -77.5) * mm, "end": v(-28.73, -77.87) * mm});
            skArc(sketch, "E21.37.0", {"start": v(-16.96, -79.77) * mm, "mid": v(-16.72, -80.65) * mm, "end": v(-16.2, -81.4) * mm});
            skLineSegment(sketch, "E21.37.1", {"start": v(-17, -79.26) * mm, "end": v(-16.96, -79.77) * mm});
            skArc(sketch, "E21.37.2", {"start": v(-17, -79.26) * mm, "mid": v(-17.1, -78.62) * mm, "end": v(-17.3, -78) * mm});
            skArc(sketch, "E21.37.3", {"start": v(-17.3, -78) * mm, "mid": v(-18.48, -76.99) * mm, "end": v(-19.99, -77.35) * mm});
            skArc(sketch, "E21.37.4", {"start": v(-20.84, -78.34) * mm, "mid": v(-20.45, -77.81) * mm, "end": v(-19.99, -77.35) * mm});
            skLineSegment(sketch, "E21.37.5", {"start": v(-20.84, -78.34) * mm, "end": v(-21.1, -78.77) * mm});
            skArc(sketch, "E21.37.6", {"start": v(-21.1, -78.77) * mm, "mid": v(-21.72, -79.45) * mm, "end": v(-22.53, -79.88) * mm});
            skArc(sketch, "E21.38.0", {"start": v(-10.65, -80.85) * mm, "mid": v(-10.34, -81.71) * mm, "end": v(-9.76, -82.42) * mm});
            skLineSegment(sketch, "E21.38.1", {"start": v(-10.73, -80.35) * mm, "end": v(-10.65, -80.85) * mm});
            skArc(sketch, "E21.38.2", {"start": v(-10.73, -80.35) * mm, "mid": v(-10.89, -79.72) * mm, "end": v(-11.13, -79.11) * mm});
            skArc(sketch, "E21.38.3", {"start": v(-11.13, -79.11) * mm, "mid": v(-12.39, -78.2) * mm, "end": v(-13.86, -78.68) * mm});
            skArc(sketch, "E21.38.4", {"start": v(-14.63, -79.73) * mm, "mid": v(-14.28, -79.18) * mm, "end": v(-13.86, -78.68) * mm});
            skLineSegment(sketch, "E21.38.5", {"start": v(-14.63, -79.73) * mm, "end": v(-14.86, -80.18) * mm});
            skArc(sketch, "E21.38.6", {"start": v(-14.86, -80.18) * mm, "mid": v(-15.42, -80.91) * mm, "end": v(-16.2, -81.4) * mm});
            skArc(sketch, "E21.39.0", {"start": v(-4.27, -81.44) * mm, "mid": v(-3.9, -82.27) * mm, "end": v(-3.26, -82.93) * mm});
            skLineSegment(sketch, "E21.39.1", {"start": v(-4.4, -80.95) * mm, "end": v(-4.27, -81.44) * mm});
            skArc(sketch, "E21.39.2", {"start": v(-4.4, -80.95) * mm, "mid": v(-4.6, -80.32) * mm, "end": v(-4.9, -79.74) * mm});
            skArc(sketch, "E21.39.3", {"start": v(-4.9, -79.74) * mm, "mid": v(-6.21, -78.93) * mm, "end": v(-7.64, -79.52) * mm});
            skArc(sketch, "E21.39.4", {"start": v(-8.33, -80.64) * mm, "mid": v(-8.03, -80.05) * mm, "end": v(-7.64, -79.52) * mm});
            skLineSegment(sketch, "E21.39.5", {"start": v(-8.33, -80.64) * mm, "end": v(-8.52, -81.1) * mm});
            skArc(sketch, "E21.39.6", {"start": v(-8.52, -81.1) * mm, "mid": v(-9.02, -81.87) * mm, "end": v(-9.76, -82.42) * mm});
            skArc(sketch, "E21.40.0", {"start": v(2.13, -81.52) * mm, "mid": v(2.57, -82.33) * mm, "end": v(3.26, -82.93) * mm});
            skLineSegment(sketch, "E21.40.1", {"start": v(1.97, -81.04) * mm, "end": v(2.13, -81.52) * mm});
            skArc(sketch, "E21.40.2", {"start": v(1.97, -81.04) * mm, "mid": v(1.72, -80.44) * mm, "end": v(1.38, -79.88) * mm});
            skArc(sketch, "E21.40.3", {"start": v(1.38, -79.88) * mm, "mid": v(0, -79.17) * mm, "end": v(-1.38, -79.88) * mm});
            skArc(sketch, "E21.40.4", {"start": v(-1.97, -81.04) * mm, "mid": v(-1.72, -80.44) * mm, "end": v(-1.38, -79.88) * mm});
            skLineSegment(sketch, "E21.40.5", {"start": v(-1.97, -81.04) * mm, "end": v(-2.13, -81.52) * mm});
            skArc(sketch, "E21.40.6", {"start": v(-2.13, -81.52) * mm, "mid": v(-2.57, -82.33) * mm, "end": v(-3.26, -82.93) * mm});
            skArc(sketch, "E21.41.0", {"start": v(8.52, -81.1) * mm, "mid": v(9.02, -81.87) * mm, "end": v(9.76, -82.42) * mm});
            skLineSegment(sketch, "E21.41.1", {"start": v(8.33, -80.64) * mm, "end": v(8.52, -81.1) * mm});
            skArc(sketch, "E21.41.2", {"start": v(8.33, -80.64) * mm, "mid": v(8.03, -80.05) * mm, "end": v(7.64, -79.52) * mm});
            skArc(sketch, "E21.41.3", {"start": v(7.64, -79.52) * mm, "mid": v(6.21, -78.93) * mm, "end": v(4.9, -79.74) * mm});
            skArc(sketch, "E21.41.4", {"start": v(4.4, -80.95) * mm, "mid": v(4.6, -80.32) * mm, "end": v(4.9, -79.74) * mm});
            skLineSegment(sketch, "E21.41.5", {"start": v(4.4, -80.95) * mm, "end": v(4.27, -81.44) * mm});
            skArc(sketch, "E21.41.6", {"start": v(4.27, -81.44) * mm, "mid": v(3.9, -82.27) * mm, "end": v(3.26, -82.93) * mm});
            skArc(sketch, "E21.42.0", {"start": v(14.86, -80.18) * mm, "mid": v(15.42, -80.91) * mm, "end": v(16.2, -81.4) * mm});
            skLineSegment(sketch, "E21.42.1", {"start": v(14.63, -79.73) * mm, "end": v(14.86, -80.18) * mm});
            skArc(sketch, "E21.42.2", {"start": v(14.63, -79.73) * mm, "mid": v(14.28, -79.18) * mm, "end": v(13.86, -78.68) * mm});
            skArc(sketch, "E21.42.3", {"start": v(13.86, -78.68) * mm, "mid": v(12.39, -78.2) * mm, "end": v(11.13, -79.11) * mm});
            skArc(sketch, "E21.42.4", {"start": v(10.73, -80.35) * mm, "mid": v(10.89, -79.72) * mm, "end": v(11.13, -79.11) * mm});
            skLineSegment(sketch, "E21.42.5", {"start": v(10.73, -80.35) * mm, "end": v(10.65, -80.85) * mm});
            skArc(sketch, "E21.42.6", {"start": v(10.65, -80.85) * mm, "mid": v(10.34, -81.71) * mm, "end": v(9.76, -82.42) * mm});
            skArc(sketch, "E21.43.0", {"start": v(21.1, -78.77) * mm, "mid": v(21.72, -79.45) * mm, "end": v(22.53, -79.88) * mm});
            skLineSegment(sketch, "E21.43.1", {"start": v(20.84, -78.34) * mm, "end": v(21.1, -78.77) * mm});
            skArc(sketch, "E21.43.2", {"start": v(20.84, -78.34) * mm, "mid": v(20.45, -77.81) * mm, "end": v(19.99, -77.35) * mm});
            skArc(sketch, "E21.43.3", {"start": v(19.99, -77.35) * mm, "mid": v(18.48, -76.99) * mm, "end": v(17.3, -78) * mm});
            skArc(sketch, "E21.43.4", {"start": v(17, -79.26) * mm, "mid": v(17.1, -78.62) * mm, "end": v(17.3, -78) * mm});
            skLineSegment(sketch, "E21.43.5", {"start": v(17, -79.26) * mm, "end": v(16.96, -79.77) * mm});
            skArc(sketch, "E21.43.6", {"start": v(16.96, -79.77) * mm, "mid": v(16.72, -80.65) * mm, "end": v(16.2, -81.4) * mm});
            skArc(sketch, "E21.44.0", {"start": v(27.22, -76.87) * mm, "mid": v(27.88, -77.5) * mm, "end": v(28.73, -77.87) * mm});
            skLineSegment(sketch, "E21.44.1", {"start": v(26.92, -76.47) * mm, "end": v(27.22, -76.87) * mm});
            skArc(sketch, "E21.44.2", {"start": v(26.92, -76.47) * mm, "mid": v(26.5, -75.97) * mm, "end": v(26, -75.54) * mm});
            skArc(sketch, "E21.44.3", {"start": v(26, -75.54) * mm, "mid": v(24.47, -75.3) * mm, "end": v(23.37, -76.4) * mm});
            skArc(sketch, "E21.44.4", {"start": v(23.17, -77.68) * mm, "mid": v(23.22, -77.03) * mm, "end": v(23.37, -76.4) * mm});
            skLineSegment(sketch, "E21.44.5", {"start": v(23.17, -77.68) * mm, "end": v(23.16, -78.19) * mm});
            skArc(sketch, "E21.44.6", {"start": v(23.16, -78.19) * mm, "mid": v(23, -79.1) * mm, "end": v(22.53, -79.88) * mm});
            skArc(sketch, "E21.45.0", {"start": v(33.17, -74.5) * mm, "mid": v(33.88, -75.08) * mm, "end": v(34.75, -75.37) * mm});
            skLineSegment(sketch, "E21.45.1", {"start": v(32.84, -74.12) * mm, "end": v(33.17, -74.5) * mm});
            skArc(sketch, "E21.45.2", {"start": v(32.84, -74.12) * mm, "mid": v(32.37, -73.66) * mm, "end": v(31.84, -73.27) * mm});
            skArc(sketch, "E21.45.3", {"start": v(31.84, -73.27) * mm, "mid": v(30.3, -73.15) * mm, "end": v(29.3, -74.33) * mm});
            skArc(sketch, "E21.45.4", {"start": v(29.2, -75.63) * mm, "mid": v(29.2, -74.97) * mm, "end": v(29.3, -74.33) * mm});
            skLineSegment(sketch, "E21.45.5", {"start": v(29.2, -75.63) * mm, "end": v(29.23, -76.13) * mm});
            skArc(sketch, "E21.45.6", {"start": v(29.23, -76.13) * mm, "mid": v(29.13, -77.04) * mm, "end": v(28.73, -77.87) * mm});
            skArc(sketch, "E21.46.0", {"start": v(38.9, -71.67) * mm, "mid": v(39.67, -72.19) * mm, "end": v(40.55, -72.41) * mm});
            skLineSegment(sketch, "E21.46.1", {"start": v(38.55, -71.31) * mm, "end": v(38.9, -71.67) * mm});
            skArc(sketch, "E21.46.2", {"start": v(38.55, -71.31) * mm, "mid": v(38.05, -70.89) * mm, "end": v(37.5, -70.55) * mm});
            skArc(sketch, "E21.46.3", {"start": v(37.5, -70.55) * mm, "mid": v(35.94, -70.54) * mm, "end": v(35.04, -71.8) * mm});
            skArc(sketch, "E21.46.4", {"start": v(35.03, -73.1) * mm, "mid": v(34.99, -72.45) * mm, "end": v(35.04, -71.8) * mm});
            skLineSegment(sketch, "E21.46.5", {"start": v(35.03, -73.1) * mm, "end": v(35.1, -73.6) * mm});
            skArc(sketch, "E21.46.6", {"start": v(35.1, -73.6) * mm, "mid": v(35.09, -74.52) * mm, "end": v(34.75, -75.37) * mm});
            skArc(sketch, "E21.47.0", {"start": v(44.41, -68.4) * mm, "mid": v(45.2, -68.85) * mm, "end": v(46.11, -69) * mm});
            skLineSegment(sketch, "E21.47.1", {"start": v(44.03, -68.07) * mm, "end": v(44.41, -68.4) * mm});
            skArc(sketch, "E21.47.2", {"start": v(44.03, -68.07) * mm, "mid": v(43.5, -67.69) * mm, "end": v(42.91, -67.39) * mm});
            skArc(sketch, "E21.47.3", {"start": v(42.91, -67.39) * mm, "mid": v(41.37, -67.5) * mm, "end": v(40.56, -68.83) * mm});
            skArc(sketch, "E21.47.4", {"start": v(40.66, -70.13) * mm, "mid": v(40.56, -69.48) * mm, "end": v(40.56, -68.83) * mm});
            skLineSegment(sketch, "E21.47.5", {"start": v(40.66, -70.13) * mm, "end": v(40.78, -70.62) * mm});
            skArc(sketch, "E21.47.6", {"start": v(40.78, -70.62) * mm, "mid": v(40.82, -71.54) * mm, "end": v(40.55, -72.41) * mm});
            skArc(sketch, "E21.48.0", {"start": v(49.64, -64.7) * mm, "mid": v(50.47, -65.1) * mm, "end": v(51.38, -65.18) * mm});
            skLineSegment(sketch, "E21.48.1", {"start": v(49.23, -64.4) * mm, "end": v(49.64, -64.7) * mm});
            skArc(sketch, "E21.48.2", {"start": v(49.23, -64.4) * mm, "mid": v(48.67, -64.06) * mm, "end": v(48.07, -63.81) * mm});
            skArc(sketch, "E21.48.3", {"start": v(48.07, -63.81) * mm, "mid": v(46.54, -64.05) * mm, "end": v(45.84, -65.43) * mm});
            skArc(sketch, "E21.48.4", {"start": v(46.04, -66.72) * mm, "mid": v(45.89, -66.09) * mm, "end": v(45.84, -65.43) * mm});
            skLineSegment(sketch, "E21.48.5", {"start": v(46.04, -66.72) * mm, "end": v(46.2, -67.2) * mm});
            skArc(sketch, "E21.48.6", {"start": v(46.2, -67.2) * mm, "mid": v(46.31, -68.11) * mm, "end": v(46.11, -69) * mm});
            skArc(sketch, "E21.49.0", {"start": v(54.57, -60.6) * mm, "mid": v(55.42, -60.93) * mm, "end": v(56.34, -60.95) * mm});
            skLineSegment(sketch, "E21.49.1", {"start": v(54.13, -60.34) * mm, "end": v(54.57, -60.6) * mm});
            skArc(sketch, "E21.49.2", {"start": v(54.13, -60.34) * mm, "mid": v(53.55, -60.05) * mm, "end": v(52.93, -59.85) * mm});
            skArc(sketch, "E21.49.3", {"start": v(52.93, -59.85) * mm, "mid": v(51.42, -60.2) * mm, "end": v(50.83, -61.64) * mm});
            skArc(sketch, "E21.49.4", {"start": v(51.13, -62.9) * mm, "mid": v(50.93, -62.28) * mm, "end": v(50.83, -61.64) * mm});
            skLineSegment(sketch, "E21.49.5", {"start": v(51.13, -62.9) * mm, "end": v(51.32, -63.37) * mm});
            skArc(sketch, "E21.49.6", {"start": v(51.32, -63.37) * mm, "mid": v(51.51, -64.27) * mm, "end": v(51.38, -65.18) * mm});
            skArc(sketch, "E21.50.0", {"start": v(59.15, -56.14) * mm, "mid": v(60.03, -56.4) * mm, "end": v(60.95, -56.34) * mm});
            skLineSegment(sketch, "E21.50.1", {"start": v(58.7, -55.9) * mm, "end": v(59.15, -56.14) * mm});
            skArc(sketch, "E21.50.2", {"start": v(58.7, -55.9) * mm, "mid": v(58.1, -55.66) * mm, "end": v(57.46, -55.5) * mm});
            skArc(sketch, "E21.50.3", {"start": v(57.46, -55.5) * mm, "mid": v(55.98, -55.98) * mm, "end": v(55.5, -57.46) * mm});
            skArc(sketch, "E21.50.4", {"start": v(55.9, -58.7) * mm, "mid": v(55.66, -58.1) * mm, "end": v(55.5, -57.46) * mm});
            skLineSegment(sketch, "E21.50.5", {"start": v(55.9, -58.7) * mm, "end": v(56.14, -59.15) * mm});
            skArc(sketch, "E21.50.6", {"start": v(56.14, -59.15) * mm, "mid": v(56.4, -60.03) * mm, "end": v(56.34, -60.95) * mm});
            skArc(sketch, "E21.51.0", {"start": v(63.37, -51.32) * mm, "mid": v(64.27, -51.51) * mm, "end": v(65.18, -51.38) * mm});
            skLineSegment(sketch, "E21.51.1", {"start": v(62.9, -51.13) * mm, "end": v(63.37, -51.32) * mm});
            skArc(sketch, "E21.51.2", {"start": v(62.9, -51.13) * mm, "mid": v(62.28, -50.93) * mm, "end": v(61.64, -50.83) * mm});
            skArc(sketch, "E21.51.3", {"start": v(61.64, -50.83) * mm, "mid": v(60.2, -51.42) * mm, "end": v(59.85, -52.93) * mm});
            skArc(sketch, "E21.51.4", {"start": v(60.34, -54.13) * mm, "mid": v(60.05, -53.55) * mm, "end": v(59.85, -52.93) * mm});
            skLineSegment(sketch, "E21.51.5", {"start": v(60.34, -54.13) * mm, "end": v(60.6, -54.57) * mm});
            skArc(sketch, "E21.51.6", {"start": v(60.6, -54.57) * mm, "mid": v(60.93, -55.42) * mm, "end": v(60.95, -56.34) * mm});
            skArc(sketch, "E21.52.0", {"start": v(67.2, -46.2) * mm, "mid": v(68.11, -46.31) * mm, "end": v(69, -46.11) * mm});
            skLineSegment(sketch, "E21.52.1", {"start": v(66.72, -46.04) * mm, "end": v(67.2, -46.2) * mm});
            skArc(sketch, "E21.52.2", {"start": v(66.72, -46.04) * mm, "mid": v(66.09, -45.89) * mm, "end": v(65.43, -45.84) * mm});
            skArc(sketch, "E21.52.3", {"start": v(65.43, -45.84) * mm, "mid": v(64.05, -46.54) * mm, "end": v(63.81, -48.07) * mm});
            skArc(sketch, "E21.52.4", {"start": v(64.4, -49.23) * mm, "mid": v(64.06, -48.67) * mm, "end": v(63.81, -48.07) * mm});
            skLineSegment(sketch, "E21.52.5", {"start": v(64.4, -49.23) * mm, "end": v(64.7, -49.64) * mm});
            skArc(sketch, "E21.52.6", {"start": v(64.7, -49.64) * mm, "mid": v(65.1, -50.47) * mm, "end": v(65.18, -51.38) * mm});
            skArc(sketch, "E21.53.0", {"start": v(70.62, -40.78) * mm, "mid": v(71.54, -40.82) * mm, "end": v(72.41, -40.55) * mm});
            skLineSegment(sketch, "E21.53.1", {"start": v(70.13, -40.66) * mm, "end": v(70.62, -40.78) * mm});
            skArc(sketch, "E21.53.2", {"start": v(70.13, -40.66) * mm, "mid": v(69.48, -40.56) * mm, "end": v(68.83, -40.56) * mm});
            skArc(sketch, "E21.53.3", {"start": v(68.83, -40.56) * mm, "mid": v(67.5, -41.37) * mm, "end": v(67.39, -42.91) * mm});
            skArc(sketch, "E21.53.4", {"start": v(68.07, -44.03) * mm, "mid": v(67.69, -43.5) * mm, "end": v(67.39, -42.91) * mm});
            skLineSegment(sketch, "E21.53.5", {"start": v(68.07, -44.03) * mm, "end": v(68.4, -44.41) * mm});
            skArc(sketch, "E21.53.6", {"start": v(68.4, -44.41) * mm, "mid": v(68.85, -45.2) * mm, "end": v(69, -46.11) * mm});
            skArc(sketch, "E21.54.0", {"start": v(73.6, -35.1) * mm, "mid": v(74.52, -35.09) * mm, "end": v(75.37, -34.75) * mm});
            skLineSegment(sketch, "E21.54.1", {"start": v(73.1, -35.03) * mm, "end": v(73.6, -35.1) * mm});
            skArc(sketch, "E21.54.2", {"start": v(73.1, -35.03) * mm, "mid": v(72.45, -34.99) * mm, "end": v(71.8, -35.04) * mm});
            skArc(sketch, "E21.54.3", {"start": v(71.8, -35.04) * mm, "mid": v(70.54, -35.94) * mm, "end": v(70.55, -37.5) * mm});
            skArc(sketch, "E21.54.4", {"start": v(71.31, -38.55) * mm, "mid": v(70.89, -38.05) * mm, "end": v(70.55, -37.5) * mm});
            skLineSegment(sketch, "E21.54.5", {"start": v(71.31, -38.55) * mm, "end": v(71.67, -38.9) * mm});
            skArc(sketch, "E21.54.6", {"start": v(71.67, -38.9) * mm, "mid": v(72.19, -39.67) * mm, "end": v(72.41, -40.55) * mm});
            skArc(sketch, "E21.55.0", {"start": v(76.13, -29.23) * mm, "mid": v(77.04, -29.13) * mm, "end": v(77.87, -28.73) * mm});
            skLineSegment(sketch, "E21.55.1", {"start": v(75.63, -29.2) * mm, "end": v(76.13, -29.23) * mm});
            skArc(sketch, "E21.55.2", {"start": v(75.63, -29.2) * mm, "mid": v(74.97, -29.2) * mm, "end": v(74.33, -29.3) * mm});
            skArc(sketch, "E21.55.3", {"start": v(74.33, -29.3) * mm, "mid": v(73.15, -30.3) * mm, "end": v(73.27, -31.84) * mm});
            skArc(sketch, "E21.55.4", {"start": v(74.12, -32.84) * mm, "mid": v(73.66, -32.37) * mm, "end": v(73.27, -31.84) * mm});
            skLineSegment(sketch, "E21.55.5", {"start": v(74.12, -32.84) * mm, "end": v(74.5, -33.17) * mm});
            skArc(sketch, "E21.55.6", {"start": v(74.5, -33.17) * mm, "mid": v(75.08, -33.88) * mm, "end": v(75.37, -34.75) * mm});
            skArc(sketch, "E21.56.0", {"start": v(78.19, -23.16) * mm, "mid": v(79.1, -23) * mm, "end": v(79.88, -22.53) * mm});
            skLineSegment(sketch, "E21.56.1", {"start": v(77.68, -23.17) * mm, "end": v(78.19, -23.16) * mm});
            skArc(sketch, "E21.56.2", {"start": v(77.68, -23.17) * mm, "mid": v(77.03, -23.22) * mm, "end": v(76.4, -23.37) * mm});
            skArc(sketch, "E21.56.3", {"start": v(76.4, -23.37) * mm, "mid": v(75.3, -24.47) * mm, "end": v(75.54, -26) * mm});
            skArc(sketch, "E21.56.4", {"start": v(76.47, -26.92) * mm, "mid": v(75.97, -26.5) * mm, "end": v(75.54, -26) * mm});
            skLineSegment(sketch, "E21.56.5", {"start": v(76.47, -26.92) * mm, "end": v(76.87, -27.22) * mm});
            skArc(sketch, "E21.56.6", {"start": v(76.87, -27.22) * mm, "mid": v(77.5, -27.88) * mm, "end": v(77.87, -28.73) * mm});
            skArc(sketch, "E21.57.0", {"start": v(79.77, -16.96) * mm, "mid": v(80.65, -16.72) * mm, "end": v(81.4, -16.2) * mm});
            skLineSegment(sketch, "E21.57.1", {"start": v(79.26, -17) * mm, "end": v(79.77, -16.96) * mm});
            skArc(sketch, "E21.57.2", {"start": v(79.26, -17) * mm, "mid": v(78.62, -17.1) * mm, "end": v(78, -17.3) * mm});
            skArc(sketch, "E21.57.3", {"start": v(78, -17.3) * mm, "mid": v(76.99, -18.48) * mm, "end": v(77.35, -19.99) * mm});
            skArc(sketch, "E21.57.4", {"start": v(78.34, -20.84) * mm, "mid": v(77.81, -20.45) * mm, "end": v(77.35, -19.99) * mm});
            skLineSegment(sketch, "E21.57.5", {"start": v(78.34, -20.84) * mm, "end": v(78.77, -21.1) * mm});
            skArc(sketch, "E21.57.6", {"start": v(78.77, -21.1) * mm, "mid": v(79.45, -21.72) * mm, "end": v(79.88, -22.53) * mm});
            skArc(sketch, "E21.58.0", {"start": v(80.85, -10.65) * mm, "mid": v(81.71, -10.34) * mm, "end": v(82.42, -9.76) * mm});
            skLineSegment(sketch, "E21.58.1", {"start": v(80.35, -10.73) * mm, "end": v(80.85, -10.65) * mm});
            skArc(sketch, "E21.58.2", {"start": v(80.35, -10.73) * mm, "mid": v(79.72, -10.89) * mm, "end": v(79.11, -11.13) * mm});
            skArc(sketch, "E21.58.3", {"start": v(79.11, -11.13) * mm, "mid": v(78.2, -12.39) * mm, "end": v(78.68, -13.86) * mm});
            skArc(sketch, "E21.58.4", {"start": v(79.73, -14.63) * mm, "mid": v(79.18, -14.28) * mm, "end": v(78.68, -13.86) * mm});
            skLineSegment(sketch, "E21.58.5", {"start": v(79.73, -14.63) * mm, "end": v(80.18, -14.86) * mm});
            skArc(sketch, "E21.58.6", {"start": v(80.18, -14.86) * mm, "mid": v(80.91, -15.42) * mm, "end": v(81.4, -16.2) * mm});
            skArc(sketch, "E21.59.0", {"start": v(81.44, -4.27) * mm, "mid": v(82.27, -3.9) * mm, "end": v(82.93, -3.26) * mm});
            skLineSegment(sketch, "E21.59.1", {"start": v(80.95, -4.4) * mm, "end": v(81.44, -4.27) * mm});
            skArc(sketch, "E21.59.2", {"start": v(80.95, -4.4) * mm, "mid": v(80.32, -4.6) * mm, "end": v(79.74, -4.9) * mm});
            skArc(sketch, "E21.59.3", {"start": v(79.74, -4.9) * mm, "mid": v(78.93, -6.21) * mm, "end": v(79.52, -7.64) * mm});
            skArc(sketch, "E21.59.4", {"start": v(80.64, -8.33) * mm, "mid": v(80.05, -8.03) * mm, "end": v(79.52, -7.64) * mm});
            skLineSegment(sketch, "E21.59.5", {"start": v(80.64, -8.33) * mm, "end": v(81.1, -8.52) * mm});
            skArc(sketch, "E21.59.6", {"start": v(81.1, -8.52) * mm, "mid": v(81.87, -9.02) * mm, "end": v(82.42, -9.76) * mm});
            skArc(sketch, "E21.60.0", {"start": v(81.52, 2.13) * mm, "mid": v(82.33, 2.57) * mm, "end": v(82.93, 3.26) * mm});
            skLineSegment(sketch, "E21.60.1", {"start": v(81.04, 1.97) * mm, "end": v(81.52, 2.13) * mm});
            skArc(sketch, "E21.60.2", {"start": v(81.04, 1.97) * mm, "mid": v(80.44, 1.72) * mm, "end": v(79.88, 1.38) * mm});
            skArc(sketch, "E21.60.3", {"start": v(79.88, 1.38) * mm, "mid": v(79.17, 0) * mm, "end": v(79.88, -1.38) * mm});
            skArc(sketch, "E21.60.4", {"start": v(81.04, -1.97) * mm, "mid": v(80.44, -1.72) * mm, "end": v(79.88, -1.38) * mm});
            skLineSegment(sketch, "E21.60.5", {"start": v(81.04, -1.97) * mm, "end": v(81.52, -2.13) * mm});
            skArc(sketch, "E21.60.6", {"start": v(81.52, -2.13) * mm, "mid": v(82.33, -2.57) * mm, "end": v(82.93, -3.26) * mm});
            skArc(sketch, "E21.61.0", {"start": v(81.1, 8.52) * mm, "mid": v(81.87, 9.02) * mm, "end": v(82.42, 9.76) * mm});
            skLineSegment(sketch, "E21.61.1", {"start": v(80.64, 8.33) * mm, "end": v(81.1, 8.52) * mm});
            skArc(sketch, "E21.61.2", {"start": v(80.64, 8.33) * mm, "mid": v(80.05, 8.03) * mm, "end": v(79.52, 7.64) * mm});
            skArc(sketch, "E21.61.3", {"start": v(79.52, 7.64) * mm, "mid": v(78.93, 6.21) * mm, "end": v(79.74, 4.9) * mm});
            skArc(sketch, "E21.61.4", {"start": v(80.95, 4.4) * mm, "mid": v(80.32, 4.6) * mm, "end": v(79.74, 4.9) * mm});
            skLineSegment(sketch, "E21.61.5", {"start": v(80.95, 4.4) * mm, "end": v(81.44, 4.27) * mm});
            skArc(sketch, "E21.61.6", {"start": v(81.44, 4.27) * mm, "mid": v(82.27, 3.9) * mm, "end": v(82.93, 3.26) * mm});
            skArc(sketch, "E21.62.0", {"start": v(80.18, 14.86) * mm, "mid": v(80.91, 15.42) * mm, "end": v(81.4, 16.2) * mm});
            skLineSegment(sketch, "E21.62.1", {"start": v(79.73, 14.63) * mm, "end": v(80.18, 14.86) * mm});
            skArc(sketch, "E21.62.2", {"start": v(79.73, 14.63) * mm, "mid": v(79.18, 14.28) * mm, "end": v(78.68, 13.86) * mm});
            skArc(sketch, "E21.62.3", {"start": v(78.68, 13.86) * mm, "mid": v(78.2, 12.39) * mm, "end": v(79.11, 11.13) * mm});
            skArc(sketch, "E21.62.4", {"start": v(80.35, 10.73) * mm, "mid": v(79.72, 10.89) * mm, "end": v(79.11, 11.13) * mm});
            skLineSegment(sketch, "E21.62.5", {"start": v(80.35, 10.73) * mm, "end": v(80.85, 10.65) * mm});
            skArc(sketch, "E21.62.6", {"start": v(80.85, 10.65) * mm, "mid": v(81.71, 10.34) * mm, "end": v(82.42, 9.76) * mm});
            skArc(sketch, "E21.63.0", {"start": v(78.77, 21.1) * mm, "mid": v(79.45, 21.72) * mm, "end": v(79.88, 22.53) * mm});
            skLineSegment(sketch, "E21.63.1", {"start": v(78.34, 20.84) * mm, "end": v(78.77, 21.1) * mm});
            skArc(sketch, "E21.63.2", {"start": v(78.34, 20.84) * mm, "mid": v(77.81, 20.45) * mm, "end": v(77.35, 19.99) * mm});
            skArc(sketch, "E21.63.3", {"start": v(77.35, 19.99) * mm, "mid": v(76.99, 18.48) * mm, "end": v(78, 17.3) * mm});
            skArc(sketch, "E21.63.4", {"start": v(79.26, 17) * mm, "mid": v(78.62, 17.1) * mm, "end": v(78, 17.3) * mm});
            skLineSegment(sketch, "E21.63.5", {"start": v(79.26, 17) * mm, "end": v(79.77, 16.96) * mm});
            skArc(sketch, "E21.63.6", {"start": v(79.77, 16.96) * mm, "mid": v(80.65, 16.72) * mm, "end": v(81.4, 16.2) * mm});
            skArc(sketch, "E21.64.0", {"start": v(76.87, 27.22) * mm, "mid": v(77.5, 27.88) * mm, "end": v(77.87, 28.73) * mm});
            skLineSegment(sketch, "E21.64.1", {"start": v(76.47, 26.92) * mm, "end": v(76.87, 27.22) * mm});
            skArc(sketch, "E21.64.2", {"start": v(76.47, 26.92) * mm, "mid": v(75.97, 26.5) * mm, "end": v(75.54, 26) * mm});
            skArc(sketch, "E21.64.3", {"start": v(75.54, 26) * mm, "mid": v(75.3, 24.47) * mm, "end": v(76.4, 23.37) * mm});
            skArc(sketch, "E21.64.4", {"start": v(77.68, 23.17) * mm, "mid": v(77.03, 23.22) * mm, "end": v(76.4, 23.37) * mm});
            skLineSegment(sketch, "E21.64.5", {"start": v(77.68, 23.17) * mm, "end": v(78.19, 23.16) * mm});
            skArc(sketch, "E21.64.6", {"start": v(78.19, 23.16) * mm, "mid": v(79.1, 23) * mm, "end": v(79.88, 22.53) * mm});
            skArc(sketch, "E21.65.0", {"start": v(74.5, 33.17) * mm, "mid": v(75.08, 33.88) * mm, "end": v(75.37, 34.75) * mm});
            skLineSegment(sketch, "E21.65.1", {"start": v(74.12, 32.84) * mm, "end": v(74.5, 33.17) * mm});
            skArc(sketch, "E21.65.2", {"start": v(74.12, 32.84) * mm, "mid": v(73.66, 32.37) * mm, "end": v(73.27, 31.84) * mm});
            skArc(sketch, "E21.65.3", {"start": v(73.27, 31.84) * mm, "mid": v(73.15, 30.3) * mm, "end": v(74.33, 29.3) * mm});
            skArc(sketch, "E21.65.4", {"start": v(75.63, 29.2) * mm, "mid": v(74.97, 29.2) * mm, "end": v(74.33, 29.3) * mm});
            skLineSegment(sketch, "E21.65.5", {"start": v(75.63, 29.2) * mm, "end": v(76.13, 29.23) * mm});
            skArc(sketch, "E21.65.6", {"start": v(76.13, 29.23) * mm, "mid": v(77.04, 29.13) * mm, "end": v(77.87, 28.73) * mm});
            skArc(sketch, "E21.66.0", {"start": v(71.67, 38.9) * mm, "mid": v(72.19, 39.67) * mm, "end": v(72.41, 40.55) * mm});
            skLineSegment(sketch, "E21.66.1", {"start": v(71.31, 38.55) * mm, "end": v(71.67, 38.9) * mm});
            skArc(sketch, "E21.66.2", {"start": v(71.31, 38.55) * mm, "mid": v(70.89, 38.05) * mm, "end": v(70.55, 37.5) * mm});
            skArc(sketch, "E21.66.3", {"start": v(70.55, 37.5) * mm, "mid": v(70.54, 35.94) * mm, "end": v(71.8, 35.04) * mm});
            skArc(sketch, "E21.66.4", {"start": v(73.1, 35.03) * mm, "mid": v(72.45, 34.99) * mm, "end": v(71.8, 35.04) * mm});
            skLineSegment(sketch, "E21.66.5", {"start": v(73.1, 35.03) * mm, "end": v(73.6, 35.1) * mm});
            skArc(sketch, "E21.66.6", {"start": v(73.6, 35.1) * mm, "mid": v(74.52, 35.09) * mm, "end": v(75.37, 34.75) * mm});
            skArc(sketch, "E21.67.0", {"start": v(68.4, 44.41) * mm, "mid": v(68.85, 45.2) * mm, "end": v(69, 46.11) * mm});
            skLineSegment(sketch, "E21.67.1", {"start": v(68.07, 44.03) * mm, "end": v(68.4, 44.41) * mm});
            skArc(sketch, "E21.67.2", {"start": v(68.07, 44.03) * mm, "mid": v(67.69, 43.5) * mm, "end": v(67.39, 42.91) * mm});
            skArc(sketch, "E21.67.3", {"start": v(67.39, 42.91) * mm, "mid": v(67.5, 41.37) * mm, "end": v(68.83, 40.56) * mm});
            skArc(sketch, "E21.67.4", {"start": v(70.13, 40.66) * mm, "mid": v(69.48, 40.56) * mm, "end": v(68.83, 40.56) * mm});
            skLineSegment(sketch, "E21.67.5", {"start": v(70.13, 40.66) * mm, "end": v(70.62, 40.78) * mm});
            skArc(sketch, "E21.67.6", {"start": v(70.62, 40.78) * mm, "mid": v(71.54, 40.82) * mm, "end": v(72.41, 40.55) * mm});
            skArc(sketch, "E21.68.0", {"start": v(64.7, 49.64) * mm, "mid": v(65.1, 50.47) * mm, "end": v(65.18, 51.38) * mm});
            skLineSegment(sketch, "E21.68.1", {"start": v(64.4, 49.23) * mm, "end": v(64.7, 49.64) * mm});
            skArc(sketch, "E21.68.2", {"start": v(64.4, 49.23) * mm, "mid": v(64.06, 48.67) * mm, "end": v(63.81, 48.07) * mm});
            skArc(sketch, "E21.68.3", {"start": v(63.81, 48.07) * mm, "mid": v(64.05, 46.54) * mm, "end": v(65.43, 45.84) * mm});
            skArc(sketch, "E21.68.4", {"start": v(66.72, 46.04) * mm, "mid": v(66.09, 45.89) * mm, "end": v(65.43, 45.84) * mm});
            skLineSegment(sketch, "E21.68.5", {"start": v(66.72, 46.04) * mm, "end": v(67.2, 46.2) * mm});
            skArc(sketch, "E21.68.6", {"start": v(67.2, 46.2) * mm, "mid": v(68.11, 46.31) * mm, "end": v(69, 46.11) * mm});
            skArc(sketch, "E21.69.0", {"start": v(60.6, 54.57) * mm, "mid": v(60.93, 55.42) * mm, "end": v(60.95, 56.34) * mm});
            skLineSegment(sketch, "E21.69.1", {"start": v(60.34, 54.13) * mm, "end": v(60.6, 54.57) * mm});
            skArc(sketch, "E21.69.2", {"start": v(60.34, 54.13) * mm, "mid": v(60.05, 53.55) * mm, "end": v(59.85, 52.93) * mm});
            skArc(sketch, "E21.69.3", {"start": v(59.85, 52.93) * mm, "mid": v(60.2, 51.42) * mm, "end": v(61.64, 50.83) * mm});
            skArc(sketch, "E21.69.4", {"start": v(62.9, 51.13) * mm, "mid": v(62.28, 50.93) * mm, "end": v(61.64, 50.83) * mm});
            skLineSegment(sketch, "E21.69.5", {"start": v(62.9, 51.13) * mm, "end": v(63.37, 51.32) * mm});
            skArc(sketch, "E21.69.6", {"start": v(63.37, 51.32) * mm, "mid": v(64.27, 51.51) * mm, "end": v(65.18, 51.38) * mm});
            skArc(sketch, "E21.70.0", {"start": v(56.14, 59.15) * mm, "mid": v(56.4, 60.03) * mm, "end": v(56.34, 60.95) * mm});
            skLineSegment(sketch, "E21.70.1", {"start": v(55.9, 58.7) * mm, "end": v(56.14, 59.15) * mm});
            skArc(sketch, "E21.70.2", {"start": v(55.9, 58.7) * mm, "mid": v(55.66, 58.1) * mm, "end": v(55.5, 57.46) * mm});
            skArc(sketch, "E21.70.3", {"start": v(55.5, 57.46) * mm, "mid": v(55.98, 55.98) * mm, "end": v(57.46, 55.5) * mm});
            skArc(sketch, "E21.70.4", {"start": v(58.7, 55.9) * mm, "mid": v(58.1, 55.66) * mm, "end": v(57.46, 55.5) * mm});
            skLineSegment(sketch, "E21.70.5", {"start": v(58.7, 55.9) * mm, "end": v(59.15, 56.14) * mm});
            skArc(sketch, "E21.70.6", {"start": v(59.15, 56.14) * mm, "mid": v(60.03, 56.4) * mm, "end": v(60.95, 56.34) * mm});
            skArc(sketch, "E21.71.0", {"start": v(51.32, 63.37) * mm, "mid": v(51.51, 64.27) * mm, "end": v(51.38, 65.18) * mm});
            skLineSegment(sketch, "E21.71.1", {"start": v(51.13, 62.9) * mm, "end": v(51.32, 63.37) * mm});
            skArc(sketch, "E21.71.2", {"start": v(51.13, 62.9) * mm, "mid": v(50.93, 62.28) * mm, "end": v(50.83, 61.64) * mm});
            skArc(sketch, "E21.71.3", {"start": v(50.83, 61.64) * mm, "mid": v(51.42, 60.2) * mm, "end": v(52.93, 59.85) * mm});
            skArc(sketch, "E21.71.4", {"start": v(54.13, 60.34) * mm, "mid": v(53.55, 60.05) * mm, "end": v(52.93, 59.85) * mm});
            skLineSegment(sketch, "E21.71.5", {"start": v(54.13, 60.34) * mm, "end": v(54.57, 60.6) * mm});
            skArc(sketch, "E21.71.6", {"start": v(54.57, 60.6) * mm, "mid": v(55.42, 60.93) * mm, "end": v(56.34, 60.95) * mm});
            skArc(sketch, "E21.72.0", {"start": v(46.2, 67.2) * mm, "mid": v(46.31, 68.11) * mm, "end": v(46.11, 69) * mm});
            skLineSegment(sketch, "E21.72.1", {"start": v(46.04, 66.72) * mm, "end": v(46.2, 67.2) * mm});
            skArc(sketch, "E21.72.2", {"start": v(46.04, 66.72) * mm, "mid": v(45.89, 66.09) * mm, "end": v(45.84, 65.43) * mm});
            skArc(sketch, "E21.72.3", {"start": v(45.84, 65.43) * mm, "mid": v(46.54, 64.05) * mm, "end": v(48.07, 63.81) * mm});
            skArc(sketch, "E21.72.4", {"start": v(49.23, 64.4) * mm, "mid": v(48.67, 64.06) * mm, "end": v(48.07, 63.81) * mm});
            skLineSegment(sketch, "E21.72.5", {"start": v(49.23, 64.4) * mm, "end": v(49.64, 64.7) * mm});
            skArc(sketch, "E21.72.6", {"start": v(49.64, 64.7) * mm, "mid": v(50.47, 65.1) * mm, "end": v(51.38, 65.18) * mm});
            skArc(sketch, "E21.73.0", {"start": v(40.78, 70.62) * mm, "mid": v(40.82, 71.54) * mm, "end": v(40.55, 72.41) * mm});
            skLineSegment(sketch, "E21.73.1", {"start": v(40.66, 70.13) * mm, "end": v(40.78, 70.62) * mm});
            skArc(sketch, "E21.73.2", {"start": v(40.66, 70.13) * mm, "mid": v(40.56, 69.48) * mm, "end": v(40.56, 68.83) * mm});
            skArc(sketch, "E21.73.3", {"start": v(40.56, 68.83) * mm, "mid": v(41.37, 67.5) * mm, "end": v(42.91, 67.39) * mm});
            skArc(sketch, "E21.73.4", {"start": v(44.03, 68.07) * mm, "mid": v(43.5, 67.69) * mm, "end": v(42.91, 67.39) * mm});
            skLineSegment(sketch, "E21.73.5", {"start": v(44.03, 68.07) * mm, "end": v(44.41, 68.4) * mm});
            skArc(sketch, "E21.73.6", {"start": v(44.41, 68.4) * mm, "mid": v(45.2, 68.85) * mm, "end": v(46.11, 69) * mm});
            skArc(sketch, "E21.74.0", {"start": v(35.1, 73.6) * mm, "mid": v(35.09, 74.52) * mm, "end": v(34.75, 75.37) * mm});
            skLineSegment(sketch, "E21.74.1", {"start": v(35.03, 73.1) * mm, "end": v(35.1, 73.6) * mm});
            skArc(sketch, "E21.74.2", {"start": v(35.03, 73.1) * mm, "mid": v(34.99, 72.45) * mm, "end": v(35.04, 71.8) * mm});
            skArc(sketch, "E21.74.3", {"start": v(35.04, 71.8) * mm, "mid": v(35.94, 70.54) * mm, "end": v(37.5, 70.55) * mm});
            skArc(sketch, "E21.74.4", {"start": v(38.55, 71.31) * mm, "mid": v(38.05, 70.89) * mm, "end": v(37.5, 70.55) * mm});
            skLineSegment(sketch, "E21.74.5", {"start": v(38.55, 71.31) * mm, "end": v(38.9, 71.67) * mm});
            skArc(sketch, "E21.74.6", {"start": v(38.9, 71.67) * mm, "mid": v(39.67, 72.19) * mm, "end": v(40.55, 72.41) * mm});
            skArc(sketch, "E21.75.0", {"start": v(29.23, 76.13) * mm, "mid": v(29.13, 77.04) * mm, "end": v(28.73, 77.87) * mm});
            skLineSegment(sketch, "E21.75.1", {"start": v(29.2, 75.63) * mm, "end": v(29.23, 76.13) * mm});
            skArc(sketch, "E21.75.2", {"start": v(29.2, 75.63) * mm, "mid": v(29.2, 74.97) * mm, "end": v(29.3, 74.33) * mm});
            skArc(sketch, "E21.75.3", {"start": v(29.3, 74.33) * mm, "mid": v(30.3, 73.15) * mm, "end": v(31.84, 73.27) * mm});
            skArc(sketch, "E21.75.4", {"start": v(32.84, 74.12) * mm, "mid": v(32.37, 73.66) * mm, "end": v(31.84, 73.27) * mm});
            skLineSegment(sketch, "E21.75.5", {"start": v(32.84, 74.12) * mm, "end": v(33.17, 74.5) * mm});
            skArc(sketch, "E21.75.6", {"start": v(33.17, 74.5) * mm, "mid": v(33.88, 75.08) * mm, "end": v(34.75, 75.37) * mm});
            skArc(sketch, "E21.76.0", {"start": v(23.16, 78.19) * mm, "mid": v(23, 79.1) * mm, "end": v(22.53, 79.88) * mm});
            skLineSegment(sketch, "E21.76.1", {"start": v(23.17, 77.68) * mm, "end": v(23.16, 78.19) * mm});
            skArc(sketch, "E21.76.2", {"start": v(23.17, 77.68) * mm, "mid": v(23.22, 77.03) * mm, "end": v(23.37, 76.4) * mm});
            skArc(sketch, "E21.76.3", {"start": v(23.37, 76.4) * mm, "mid": v(24.47, 75.3) * mm, "end": v(26, 75.54) * mm});
            skArc(sketch, "E21.76.4", {"start": v(26.92, 76.47) * mm, "mid": v(26.5, 75.97) * mm, "end": v(26, 75.54) * mm});
            skLineSegment(sketch, "E21.76.5", {"start": v(26.92, 76.47) * mm, "end": v(27.22, 76.87) * mm});
            skArc(sketch, "E21.76.6", {"start": v(27.22, 76.87) * mm, "mid": v(27.88, 77.5) * mm, "end": v(28.73, 77.87) * mm});
            skArc(sketch, "E21.77.0", {"start": v(16.96, 79.77) * mm, "mid": v(16.72, 80.65) * mm, "end": v(16.2, 81.4) * mm});
            skLineSegment(sketch, "E21.77.1", {"start": v(17, 79.26) * mm, "end": v(16.96, 79.77) * mm});
            skArc(sketch, "E21.77.2", {"start": v(17, 79.26) * mm, "mid": v(17.1, 78.62) * mm, "end": v(17.3, 78) * mm});
            skArc(sketch, "E21.77.3", {"start": v(17.3, 78) * mm, "mid": v(18.48, 76.99) * mm, "end": v(19.99, 77.35) * mm});
            skArc(sketch, "E21.77.4", {"start": v(20.84, 78.34) * mm, "mid": v(20.45, 77.81) * mm, "end": v(19.99, 77.35) * mm});
            skLineSegment(sketch, "E21.77.5", {"start": v(20.84, 78.34) * mm, "end": v(21.1, 78.77) * mm});
            skArc(sketch, "E21.77.6", {"start": v(21.1, 78.77) * mm, "mid": v(21.72, 79.45) * mm, "end": v(22.53, 79.88) * mm});
            skArc(sketch, "E21.78.0", {"start": v(10.65, 80.85) * mm, "mid": v(10.34, 81.71) * mm, "end": v(9.76, 82.42) * mm});
            skLineSegment(sketch, "E21.78.1", {"start": v(10.73, 80.35) * mm, "end": v(10.65, 80.85) * mm});
            skArc(sketch, "E21.78.2", {"start": v(10.73, 80.35) * mm, "mid": v(10.89, 79.72) * mm, "end": v(11.13, 79.11) * mm});
            skArc(sketch, "E21.78.3", {"start": v(11.13, 79.11) * mm, "mid": v(12.39, 78.2) * mm, "end": v(13.86, 78.68) * mm});
            skArc(sketch, "E21.78.4", {"start": v(14.63, 79.73) * mm, "mid": v(14.28, 79.18) * mm, "end": v(13.86, 78.68) * mm});
            skLineSegment(sketch, "E21.78.5", {"start": v(14.63, 79.73) * mm, "end": v(14.86, 80.18) * mm});
            skArc(sketch, "E21.78.6", {"start": v(14.86, 80.18) * mm, "mid": v(15.42, 80.91) * mm, "end": v(16.2, 81.4) * mm});
            skArc(sketch, "E21.79.0", {"start": v(4.27, 81.44) * mm, "mid": v(3.9, 82.27) * mm, "end": v(3.26, 82.93) * mm});
            skLineSegment(sketch, "E21.79.1", {"start": v(4.4, 80.95) * mm, "end": v(4.27, 81.44) * mm});
            skArc(sketch, "E21.79.2", {"start": v(4.4, 80.95) * mm, "mid": v(4.6, 80.32) * mm, "end": v(4.9, 79.74) * mm});
            skArc(sketch, "E21.79.3", {"start": v(4.9, 79.74) * mm, "mid": v(6.21, 78.93) * mm, "end": v(7.64, 79.52) * mm});
            skArc(sketch, "E21.79.4", {"start": v(8.33, 80.64) * mm, "mid": v(8.03, 80.05) * mm, "end": v(7.64, 79.52) * mm});
            skLineSegment(sketch, "E21.79.5", {"start": v(8.33, 80.64) * mm, "end": v(8.52, 81.1) * mm});
            skArc(sketch, "E21.79.6", {"start": v(8.52, 81.1) * mm, "mid": v(9.02, 81.87) * mm, "end": v(9.76, 82.42) * mm});
            skSolve(sketch);
        }
        {
            var Q0;
            Q0 = qSketchRegion(id + "F2", true);
            extrude(context, id + "F3", {"entities" : qUnion([Q0]), "operationType" : NewBodyOperationType.INTERSECT, "endBound" : BoundingType.THROUGH_ALL, "oppositeDirection" : true, "depth" : 25.4 * mm});
        }
        {
            var Q0;
            Q0=makeQuery(id+"F1.opExtrude","CAP_FACE",FACE,{"disambiguationData":[OSD([sQuery(id+"F0.wireOp",EDGE,"E0"),sQuery(id+"F0.wireOp",EDGE,"E1")])],"isStart":false});
            var sketch = newSketch(context, id + "F4", { "sketchPlane" : qUnion([Q0])});
            skCircle(sketch, "E22", {"center": v(0, 0) * mm, "radius": 32.28 * mm, "construction": true});
            skCircle(sketch, "E23", {"center": v(0, 0) * mm, "radius": 72.17 * mm, "construction": true});
            skCircle(sketch, "E24", {"center": v(0, 72.17) * mm, "radius": 2.7 * mm});
            skCircle(sketch, "E25.1.0", {"center": v(-72.17, 0) * mm, "radius": 2.7 * mm});
            skCircle(sketch, "E25.2.0", {"center": v(0, -72.17) * mm, "radius": 2.7 * mm});
            skCircle(sketch, "E25.3.0", {"center": v(72.17, 0) * mm, "radius": 2.7 * mm});
            skCircle(sketch, "E26", {"center": v(0, 32.28) * mm, "radius": 3.3 * mm});
            skCircle(sketch, "E27.1.0", {"center": v(-32.28, 0) * mm, "radius": 3.3 * mm});
            skCircle(sketch, "E27.2.0", {"center": v(0, -32.28) * mm, "radius": 3.3 * mm});
            skCircle(sketch, "E27.3.0", {"center": v(32.28, 0) * mm, "radius": 3.3 * mm});
            skSolve(sketch);
        }
        {
            var Q0;
            Q0 = qSketchRegion(id + "F4", true);
            extrude(context, id + "F5", {"entities" : qUnion([Q0]), "operationType" : NewBodyOperationType.REMOVE, "endBound" : BoundingType.THROUGH_ALL, "oppositeDirection" : true, "depth" : 25.4 * mm});
        }
        {
            var Q0;
            Q0=makeQuery(id+"F1.opExtrude","CAP_FACE",FACE,{"disambiguationData":[OSD([sQuery(id+"F0.wireOp",EDGE,"E0"),sQuery(id+"F0.wireOp",EDGE,"E1")])],"isStart":false});
            var sketch = newSketch(context, id + "F6", { "sketchPlane" : qUnion([Q0])});
            skLineSegment(sketch, "E28", {"start": v(0, 0) * mm, "end": v(73.69, 73.69) * mm, "construction": true});
            skLineSegment(sketch, "E29", {"start": v(0, 0) * mm, "end": v(25.27, 43.77) * mm, "construction": true});
            skLineSegment(sketch, "E30", {"start": v(0, 0) * mm, "end": v(43.77, 25.27) * mm, "construction": true});
            skLineSegment(sketch, "E31", {"start": v(33.21, 57.52) * mm, "end": v(47, 81.41) * mm, "construction": true});
            skLineSegment(sketch, "E32", {"start": v(25.27, 43.77) * mm, "end": v(33.21, 57.52) * mm, "construction": true});
            skLineSegment(sketch, "E33", {"start": v(43.77, 25.27) * mm, "end": v(81.41, 47) * mm, "construction": true});
            skArc(sketch, "E34", {"start": v(57.52, 33.21) * mm, "mid": v(46.97, 46.97) * mm, "end": v(33.21, 57.52) * mm});
            skArc(sketch, "E35", {"start": v(33.21, 57.52) * mm, "mid": v(-46.97, -46.97) * mm, "end": v(57.52, 33.21) * mm, "construction": true});
            skArc(sketch, "E36", {"start": v(25.27, 43.77) * mm, "mid": v(-35.74, -35.74) * mm, "end": v(43.77, 25.27) * mm, "construction": true});
            skArc(sketch, "E37", {"start": v(43.77, 25.27) * mm, "mid": v(35.74, 35.74) * mm, "end": v(25.27, 43.77) * mm});
            skArc(sketch, "E38", {"start": v(25.27, 43.77) * mm, "mid": v(22.37, 54.62) * mm, "end": v(33.21, 57.52) * mm});
            skArc(sketch, "E39", {"start": v(43.77, 25.27) * mm, "mid": v(54.62, 22.37) * mm, "end": v(57.52, 33.21) * mm});
            skCircle(sketch, "E40", {"center": v(35.74, 35.74) * mm, "radius": 7.94 * mm});
            skCircle(sketch, "E41.1.0", {"center": v(-35.74, 35.74) * mm, "radius": 7.94 * mm});
            skArc(sketch, "E41.1.1", {"start": v(-25.27, 43.77) * mm, "mid": v(-22.37, 54.62) * mm, "end": v(-33.21, 57.52) * mm});
            skArc(sketch, "E41.1.2", {"start": v(-43.77, 25.27) * mm, "mid": v(-54.62, 22.37) * mm, "end": v(-57.52, 33.21) * mm});
            skArc(sketch, "E41.1.3", {"start": v(-25.27, 43.77) * mm, "mid": v(-35.74, 35.74) * mm, "end": v(-43.77, 25.27) * mm});
            skLineSegment(sketch, "E41.1.4", {"start": v(-43.77, 25.27) * mm, "end": v(-57.52, 33.21) * mm, "construction": true});
            skArc(sketch, "E41.1.5", {"start": v(-33.21, 57.52) * mm, "mid": v(-46.97, 46.97) * mm, "end": v(-57.52, 33.21) * mm});
            skCircle(sketch, "E41.2.0", {"center": v(-35.74, -35.74) * mm, "radius": 7.94 * mm});
            skArc(sketch, "E41.2.1", {"start": v(-43.77, -25.27) * mm, "mid": v(-54.62, -22.37) * mm, "end": v(-57.52, -33.21) * mm});
            skArc(sketch, "E41.2.2", {"start": v(-25.27, -43.77) * mm, "mid": v(-22.37, -54.62) * mm, "end": v(-33.21, -57.52) * mm});
            skArc(sketch, "E41.2.3", {"start": v(-43.77, -25.27) * mm, "mid": v(-35.74, -35.74) * mm, "end": v(-25.27, -43.77) * mm});
            skLineSegment(sketch, "E41.2.4", {"start": v(-25.27, -43.77) * mm, "end": v(-33.21, -57.52) * mm, "construction": true});
            skArc(sketch, "E41.2.5", {"start": v(-57.52, -33.21) * mm, "mid": v(-46.97, -46.97) * mm, "end": v(-33.21, -57.52) * mm});
            skCircle(sketch, "E41.3.0", {"center": v(35.74, -35.74) * mm, "radius": 7.94 * mm});
            skArc(sketch, "E41.3.1", {"start": v(25.27, -43.77) * mm, "mid": v(22.37, -54.62) * mm, "end": v(33.21, -57.52) * mm});
            skArc(sketch, "E41.3.2", {"start": v(43.77, -25.27) * mm, "mid": v(54.62, -22.37) * mm, "end": v(57.52, -33.21) * mm});
            skArc(sketch, "E41.3.3", {"start": v(25.27, -43.77) * mm, "mid": v(35.74, -35.74) * mm, "end": v(43.77, -25.27) * mm});
            skLineSegment(sketch, "E41.3.4", {"start": v(43.77, -25.27) * mm, "end": v(57.52, -33.21) * mm, "construction": true});
            skArc(sketch, "E41.3.5", {"start": v(33.21, -57.52) * mm, "mid": v(46.97, -46.97) * mm, "end": v(57.52, -33.21) * mm});
            skSolve(sketch);
        }
        {
            var Q0;
            Q0 = qSketchRegion(id + "F6", true);
            extrude(context, id + "F7", {"entities" : qUnion([Q0]), "operationType" : NewBodyOperationType.REMOVE, "endBound" : BoundingType.THROUGH_ALL, "oppositeDirection" : true, "depth" : 25.4 * mm});
        }
        {
            var Q0;
            {var subQ0=sQuery(id+"F6.wireOp",EDGE,"E40");var subQ1=sQuery(id+"F6.wireOp",EDGE,"E37");Q0=makeQuery(id+"F7.boolean.opBoolean","COPY",EDGE,{"derivedFrom":makeQuery(id+"F7.opExtrude","SWEPT_EDGE",EDGE,{"disambiguationData":[OSD([subQ1,subQ0]),TDD([makeQuery(id+"F6.imprint","INTERSECT",VERTEX,{"disambiguationData":[OD(1.0)],"derivedFrom":[subQ1,subQ0]})])]})});}
            var Q1;
            {var subQ0=sQuery(id+"F6.wireOp",EDGE,"E40");var subQ1=sQuery(id+"F6.wireOp",EDGE,"E37");Q1=makeQuery(id+"F7.boolean.opBoolean","COPY",EDGE,{"derivedFrom":makeQuery(id+"F7.opExtrude","SWEPT_EDGE",EDGE,{"disambiguationData":[OSD([subQ1,subQ0]),TDD([makeQuery(id+"F6.imprint","INTERSECT",VERTEX,{"disambiguationData":[OD(0.0)],"derivedFrom":[subQ1,subQ0]})])]})});}
            var Q2;
            {var subQ0=sQuery(id+"F6.wireOp",EDGE,"E41.3.3");var subQ1=sQuery(id+"F6.wireOp",EDGE,"E41.3.0");Q2=makeQuery(id+"F7.boolean.opBoolean","COPY",EDGE,{"derivedFrom":makeQuery(id+"F7.opExtrude","SWEPT_EDGE",EDGE,{"disambiguationData":[OSD([subQ1,subQ0]),TDD([makeQuery(id+"F6.imprint","INTERSECT",VERTEX,{"disambiguationData":[OD(1.0)],"derivedFrom":[subQ1,subQ0]})])]})});}
            var Q3;
            {var subQ0=sQuery(id+"F6.wireOp",EDGE,"E41.3.3");var subQ1=sQuery(id+"F6.wireOp",EDGE,"E41.3.0");Q3=makeQuery(id+"F7.boolean.opBoolean","COPY",EDGE,{"derivedFrom":makeQuery(id+"F7.opExtrude","SWEPT_EDGE",EDGE,{"disambiguationData":[OSD([subQ1,subQ0]),TDD([makeQuery(id+"F6.imprint","INTERSECT",VERTEX,{"disambiguationData":[OD(0.0)],"derivedFrom":[subQ1,subQ0]})])]})});}
            var Q4;
            {var subQ0=sQuery(id+"F6.wireOp",EDGE,"E41.2.3");var subQ1=sQuery(id+"F6.wireOp",EDGE,"E41.2.0");Q4=makeQuery(id+"F7.boolean.opBoolean","COPY",EDGE,{"derivedFrom":makeQuery(id+"F7.opExtrude","SWEPT_EDGE",EDGE,{"disambiguationData":[OSD([subQ1,subQ0]),TDD([makeQuery(id+"F6.imprint","INTERSECT",VERTEX,{"disambiguationData":[OD(1.0)],"derivedFrom":[subQ1,subQ0]})])]})});}
            var Q5;
            {var subQ0=sQuery(id+"F6.wireOp",EDGE,"E41.2.3");var subQ1=sQuery(id+"F6.wireOp",EDGE,"E41.2.0");Q5=makeQuery(id+"F7.boolean.opBoolean","COPY",EDGE,{"derivedFrom":makeQuery(id+"F7.opExtrude","SWEPT_EDGE",EDGE,{"disambiguationData":[OSD([subQ1,subQ0]),TDD([makeQuery(id+"F6.imprint","INTERSECT",VERTEX,{"disambiguationData":[OD(0.0)],"derivedFrom":[subQ1,subQ0]})])]})});}
            var Q6;
            {var subQ0=sQuery(id+"F6.wireOp",EDGE,"E41.1.3");var subQ1=sQuery(id+"F6.wireOp",EDGE,"E41.1.0");Q6=makeQuery(id+"F7.boolean.opBoolean","COPY",EDGE,{"derivedFrom":makeQuery(id+"F7.opExtrude","SWEPT_EDGE",EDGE,{"disambiguationData":[OSD([subQ1,subQ0]),TDD([makeQuery(id+"F6.imprint","INTERSECT",VERTEX,{"disambiguationData":[OD(0.0)],"derivedFrom":[subQ1,subQ0]})])]})});}
            var Q7;
            {var subQ0=sQuery(id+"F6.wireOp",EDGE,"E41.1.3");var subQ1=sQuery(id+"F6.wireOp",EDGE,"E41.1.0");Q7=makeQuery(id+"F7.boolean.opBoolean","COPY",EDGE,{"derivedFrom":makeQuery(id+"F7.opExtrude","SWEPT_EDGE",EDGE,{"disambiguationData":[OSD([subQ1,subQ0]),TDD([makeQuery(id+"F6.imprint","INTERSECT",VERTEX,{"disambiguationData":[OD(1.0)],"derivedFrom":[subQ1,subQ0]})])]})});}
            fillet(context, id + "F8", {"entities" : qUnion([Q0, Q1, Q2, Q3, Q4, Q5, Q6, Q7]), "radius" : 10.16 * mm, "tangentPropagation" : true, "allowEdgeOverflow" : false});
        }
    });
